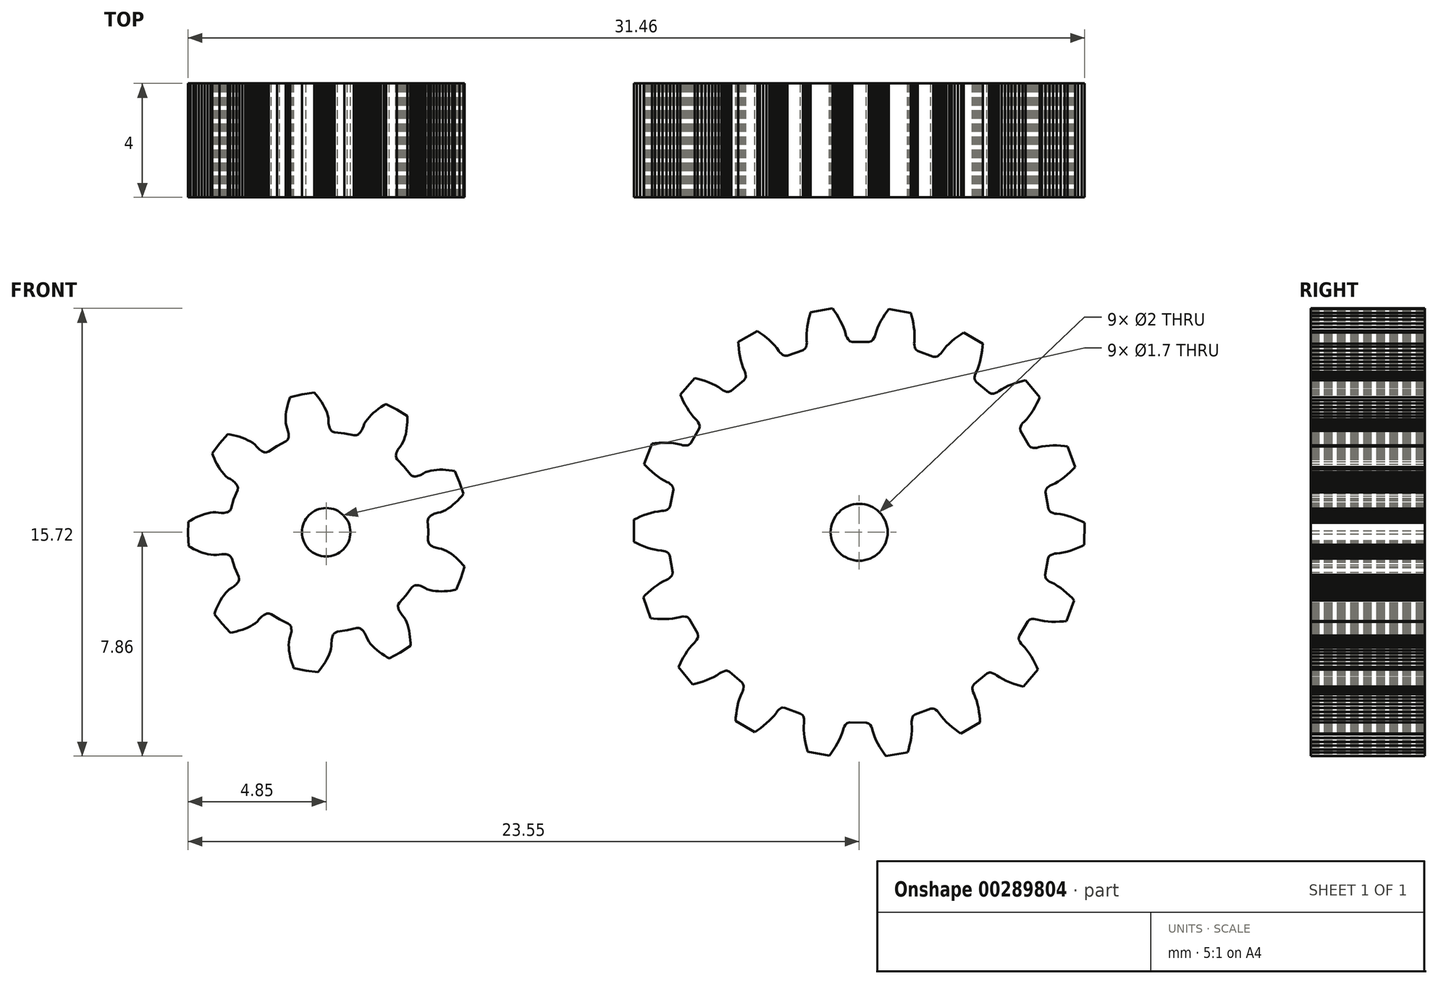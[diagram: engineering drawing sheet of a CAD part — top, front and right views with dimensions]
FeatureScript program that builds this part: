
annotation { "Feature Type Name" : "Feature", "Feature Type Description" : "" }
export const myFeature = defineFeature(function(context is Context, id is Id, definition is map)
    precondition{}
    {
        {
            var Q0;
            Q0=qCreatedBy(makeId("Front.planeOp"),FACE);
            var sketch = newSketch(context, id + "F0", { "sketchPlane" : qUnion([Q0])});
            skLineSegment(sketch, "E0", {"start": v(3.58, -0.29) * mm, "end": v(3.6, -0.37) * mm});
            skLineSegment(sketch, "E1", {"start": v(3.6, -0.37) * mm, "end": v(3.61, -0.4) * mm});
            skLineSegment(sketch, "E2", {"start": v(3.61, -0.4) * mm, "end": v(3.63, -0.43) * mm});
            skLineSegment(sketch, "E3", {"start": v(3.63, -0.43) * mm, "end": v(3.65, -0.45) * mm});
            skLineSegment(sketch, "E4", {"start": v(3.65, -0.45) * mm, "end": v(3.67, -0.46) * mm});
            skLineSegment(sketch, "E5", {"start": v(3.67, -0.46) * mm, "end": v(3.72, -0.5) * mm});
            skLineSegment(sketch, "E6", {"start": v(3.72, -0.5) * mm, "end": v(3.76, -0.51) * mm});
            skLineSegment(sketch, "E7", {"start": v(3.76, -0.51) * mm, "end": v(3.8, -0.53) * mm});
            skLineSegment(sketch, "E8", {"start": v(3.8, -0.53) * mm, "end": v(3.85, -0.54) * mm});
            skLineSegment(sketch, "E9", {"start": v(3.85, -0.54) * mm, "end": v(3.95, -0.56) * mm});
            skLineSegment(sketch, "E10", {"start": v(3.95, -0.56) * mm, "end": v(4.04, -0.58) * mm});
            skLineSegment(sketch, "E11", {"start": v(4.04, -0.58) * mm, "end": v(4.13, -0.61) * mm});
            skLineSegment(sketch, "E12", {"start": v(4.13, -0.61) * mm, "end": v(4.22, -0.66) * mm});
            skLineSegment(sketch, "E13", {"start": v(4.22, -0.66) * mm, "end": v(4.3, -0.7) * mm});
            skLineSegment(sketch, "E14", {"start": v(4.3, -0.7) * mm, "end": v(4.4, -0.76) * mm});
            skLineSegment(sketch, "E15", {"start": v(4.4, -0.76) * mm, "end": v(4.47, -0.83) * mm});
            skLineSegment(sketch, "E16", {"start": v(4.47, -0.83) * mm, "end": v(4.56, -0.9) * mm});
            skLineSegment(sketch, "E17", {"start": v(4.56, -0.9) * mm, "end": v(4.64, -0.97) * mm});
            skLineSegment(sketch, "E18", {"start": v(4.64, -0.97) * mm, "end": v(4.72, -1.05) * mm});
            skLineSegment(sketch, "E19", {"start": v(4.72, -1.05) * mm, "end": v(4.8, -1.13) * mm});
            skLineSegment(sketch, "E20", {"start": v(4.8, -1.13) * mm, "end": v(4.85, -1.2) * mm});
            skLineSegment(sketch, "E21", {"start": v(4.85, -1.2) * mm, "end": v(4.73, -1.61) * mm});
            skLineSegment(sketch, "E22", {"start": v(4.73, -1.61) * mm, "end": v(4.57, -2.01) * mm});
            skLineSegment(sketch, "E23", {"start": v(4.57, -2.01) * mm, "end": v(4.48, -2.03) * mm});
            skLineSegment(sketch, "E24", {"start": v(4.48, -2.03) * mm, "end": v(4.37, -2.05) * mm});
            skLineSegment(sketch, "E25", {"start": v(4.37, -2.05) * mm, "end": v(4.26, -2.06) * mm});
            skLineSegment(sketch, "E26", {"start": v(4.26, -2.06) * mm, "end": v(4.15, -2.07) * mm});
            skLineSegment(sketch, "E27", {"start": v(4.15, -2.07) * mm, "end": v(4.04, -2.07) * mm});
            skLineSegment(sketch, "E28", {"start": v(4.04, -2.07) * mm, "end": v(3.94, -2.07) * mm});
            skLineSegment(sketch, "E29", {"start": v(3.94, -2.07) * mm, "end": v(3.83, -2.06) * mm});
            skLineSegment(sketch, "E30", {"start": v(3.83, -2.06) * mm, "end": v(3.73, -2.05) * mm});
            skLineSegment(sketch, "E31", {"start": v(3.73, -2.05) * mm, "end": v(3.64, -2.03) * mm});
            skLineSegment(sketch, "E32", {"start": v(3.64, -2.03) * mm, "end": v(3.55, -2) * mm});
            skLineSegment(sketch, "E33", {"start": v(3.55, -2) * mm, "end": v(3.46, -1.95) * mm});
            skLineSegment(sketch, "E34", {"start": v(3.46, -1.95) * mm, "end": v(3.38, -1.9) * mm});
            skLineSegment(sketch, "E35", {"start": v(3.38, -1.9) * mm, "end": v(3.33, -1.9) * mm});
            skLineSegment(sketch, "E36", {"start": v(3.33, -1.9) * mm, "end": v(3.29, -1.88) * mm});
            skLineSegment(sketch, "E37", {"start": v(3.29, -1.88) * mm, "end": v(3.24, -1.87) * mm});
            skLineSegment(sketch, "E38", {"start": v(3.24, -1.87) * mm, "end": v(3.19, -1.86) * mm});
            skLineSegment(sketch, "E39", {"start": v(3.19, -1.86) * mm, "end": v(3.16, -1.86) * mm});
            skLineSegment(sketch, "E40", {"start": v(3.16, -1.86) * mm, "end": v(3.13, -1.86) * mm});
            skLineSegment(sketch, "E41", {"start": v(3.13, -1.86) * mm, "end": v(3.1, -1.87) * mm});
            skLineSegment(sketch, "E42", {"start": v(3.1, -1.87) * mm, "end": v(3.06, -1.88) * mm});
            skLineSegment(sketch, "E43", {"start": v(3.06, -1.88) * mm, "end": v(3, -1.94) * mm});
            skLineSegment(sketch, "E44", {"start": v(3, -1.94) * mm, "end": v(2.8, -2.21) * mm});
            skLineSegment(sketch, "E45", {"start": v(2.8, -2.21) * mm, "end": v(2.57, -2.47) * mm});
            skLineSegment(sketch, "E46", {"start": v(2.57, -2.47) * mm, "end": v(2.53, -2.54) * mm});
            skLineSegment(sketch, "E47", {"start": v(2.53, -2.54) * mm, "end": v(2.52, -2.58) * mm});
            skLineSegment(sketch, "E48", {"start": v(2.52, -2.58) * mm, "end": v(2.52, -2.61) * mm});
            skLineSegment(sketch, "E49", {"start": v(2.52, -2.61) * mm, "end": v(2.52, -2.64) * mm});
            skLineSegment(sketch, "E50", {"start": v(2.52, -2.64) * mm, "end": v(2.53, -2.67) * mm});
            skLineSegment(sketch, "E51", {"start": v(2.53, -2.67) * mm, "end": v(2.55, -2.72) * mm});
            skLineSegment(sketch, "E52", {"start": v(2.55, -2.72) * mm, "end": v(2.57, -2.76) * mm});
            skLineSegment(sketch, "E53", {"start": v(2.57, -2.76) * mm, "end": v(2.59, -2.8) * mm});
            skLineSegment(sketch, "E54", {"start": v(2.59, -2.8) * mm, "end": v(2.62, -2.84) * mm});
            skLineSegment(sketch, "E55", {"start": v(2.62, -2.84) * mm, "end": v(2.67, -2.92) * mm});
            skLineSegment(sketch, "E56", {"start": v(2.67, -2.92) * mm, "end": v(2.74, -3) * mm});
            skLineSegment(sketch, "E57", {"start": v(2.74, -3) * mm, "end": v(2.78, -3.07) * mm});
            skLineSegment(sketch, "E58", {"start": v(2.78, -3.07) * mm, "end": v(2.82, -3.16) * mm});
            skLineSegment(sketch, "E59", {"start": v(2.82, -3.16) * mm, "end": v(2.86, -3.26) * mm});
            skLineSegment(sketch, "E60", {"start": v(2.86, -3.26) * mm, "end": v(2.89, -3.36) * mm});
            skLineSegment(sketch, "E61", {"start": v(2.89, -3.36) * mm, "end": v(2.9, -3.46) * mm});
            skLineSegment(sketch, "E62", {"start": v(2.9, -3.46) * mm, "end": v(2.93, -3.57) * mm});
            skLineSegment(sketch, "E63", {"start": v(2.93, -3.57) * mm, "end": v(2.94, -3.68) * mm});
            skLineSegment(sketch, "E64", {"start": v(2.94, -3.68) * mm, "end": v(2.95, -3.79) * mm});
            skLineSegment(sketch, "E65", {"start": v(2.95, -3.79) * mm, "end": v(2.96, -3.9) * mm});
            skLineSegment(sketch, "E66", {"start": v(2.96, -3.9) * mm, "end": v(2.96, -3.99) * mm});
            skLineSegment(sketch, "E67", {"start": v(2.96, -3.99) * mm, "end": v(2.6, -4.23) * mm});
            skLineSegment(sketch, "E68", {"start": v(2.6, -4.23) * mm, "end": v(2.22, -4.43) * mm});
            skLineSegment(sketch, "E69", {"start": v(2.22, -4.43) * mm, "end": v(2.14, -4.39) * mm});
            skLineSegment(sketch, "E70", {"start": v(2.14, -4.39) * mm, "end": v(2.04, -4.33) * mm});
            skLineSegment(sketch, "E71", {"start": v(2.04, -4.33) * mm, "end": v(1.95, -4.27) * mm});
            skLineSegment(sketch, "E72", {"start": v(1.95, -4.27) * mm, "end": v(1.86, -4.2) * mm});
            skLineSegment(sketch, "E73", {"start": v(1.86, -4.2) * mm, "end": v(1.78, -4.14) * mm});
            skLineSegment(sketch, "E74", {"start": v(1.78, -4.14) * mm, "end": v(1.7, -4.07) * mm});
            skLineSegment(sketch, "E75", {"start": v(1.7, -4.07) * mm, "end": v(1.62, -4) * mm});
            skLineSegment(sketch, "E76", {"start": v(1.62, -4) * mm, "end": v(1.56, -3.92) * mm});
            skLineSegment(sketch, "E77", {"start": v(1.56, -3.92) * mm, "end": v(1.5, -3.84) * mm});
            skLineSegment(sketch, "E78", {"start": v(1.5, -3.84) * mm, "end": v(1.45, -3.76) * mm});
            skLineSegment(sketch, "E79", {"start": v(1.45, -3.76) * mm, "end": v(1.41, -3.67) * mm});
            skLineSegment(sketch, "E80", {"start": v(1.41, -3.67) * mm, "end": v(1.37, -3.59) * mm});
            skLineSegment(sketch, "E81", {"start": v(1.37, -3.59) * mm, "end": v(1.35, -3.54) * mm});
            skLineSegment(sketch, "E82", {"start": v(1.35, -3.54) * mm, "end": v(1.33, -3.5) * mm});
            skLineSegment(sketch, "E83", {"start": v(1.33, -3.5) * mm, "end": v(1.3, -3.46) * mm});
            skLineSegment(sketch, "E84", {"start": v(1.3, -3.46) * mm, "end": v(1.26, -3.43) * mm});
            skLineSegment(sketch, "E85", {"start": v(1.26, -3.43) * mm, "end": v(1.24, -3.4) * mm});
            skLineSegment(sketch, "E86", {"start": v(1.24, -3.4) * mm, "end": v(1.21, -3.4) * mm});
            skLineSegment(sketch, "E87", {"start": v(1.21, -3.4) * mm, "end": v(1.19, -3.38) * mm});
            skLineSegment(sketch, "E88", {"start": v(1.19, -3.38) * mm, "end": v(1.15, -3.36) * mm});
            skLineSegment(sketch, "E89", {"start": v(1.15, -3.36) * mm, "end": v(1.07, -3.36) * mm});
            skLineSegment(sketch, "E90", {"start": v(1.07, -3.36) * mm, "end": v(0.73, -3.44) * mm});
            skLineSegment(sketch, "E91", {"start": v(0.73, -3.44) * mm, "end": v(0.4, -3.5) * mm});
            skLineSegment(sketch, "E92", {"start": v(0.4, -3.5) * mm, "end": v(0.31, -3.52) * mm});
            skLineSegment(sketch, "E93", {"start": v(0.31, -3.52) * mm, "end": v(0.29, -3.55) * mm});
            skLineSegment(sketch, "E94", {"start": v(0.29, -3.55) * mm, "end": v(0.27, -3.57) * mm});
            skLineSegment(sketch, "E95", {"start": v(0.27, -3.57) * mm, "end": v(0.25, -3.6) * mm});
            skLineSegment(sketch, "E96", {"start": v(0.25, -3.6) * mm, "end": v(0.24, -3.62) * mm});
            skLineSegment(sketch, "E97", {"start": v(0.24, -3.62) * mm, "end": v(0.22, -3.67) * mm});
            skLineSegment(sketch, "E98", {"start": v(0.22, -3.67) * mm, "end": v(0.2, -3.72) * mm});
            skLineSegment(sketch, "E99", {"start": v(0.2, -3.72) * mm, "end": v(0.2, -3.76) * mm});
            skLineSegment(sketch, "E100", {"start": v(0.2, -3.76) * mm, "end": v(0.19, -3.81) * mm});
            skLineSegment(sketch, "E101", {"start": v(0.19, -3.81) * mm, "end": v(0.19, -3.9) * mm});
            skLineSegment(sketch, "E102", {"start": v(0.19, -3.9) * mm, "end": v(0.19, -4) * mm});
            skLineSegment(sketch, "E103", {"start": v(0.19, -4) * mm, "end": v(0.17, -4.1) * mm});
            skLineSegment(sketch, "E104", {"start": v(0.17, -4.1) * mm, "end": v(0.14, -4.19) * mm});
            skLineSegment(sketch, "E105", {"start": v(0.14, -4.19) * mm, "end": v(0.1, -4.28) * mm});
            skLineSegment(sketch, "E106", {"start": v(0.1, -4.28) * mm, "end": v(0.07, -4.38) * mm});
            skLineSegment(sketch, "E107", {"start": v(0.07, -4.38) * mm, "end": v(0.02, -4.47) * mm});
            skLineSegment(sketch, "E108", {"start": v(0.02, -4.47) * mm, "end": v(-0.04, -4.57) * mm});
            skLineSegment(sketch, "E109", {"start": v(-0.04, -4.57) * mm, "end": v(-0.1, -4.66) * mm});
            skLineSegment(sketch, "E110", {"start": v(-0.1, -4.66) * mm, "end": v(-0.16, -4.75) * mm});
            skLineSegment(sketch, "E111", {"start": v(-0.16, -4.75) * mm, "end": v(-0.23, -4.84) * mm});
            skLineSegment(sketch, "E112", {"start": v(-0.23, -4.84) * mm, "end": v(-0.28, -4.9) * mm});
            skLineSegment(sketch, "E113", {"start": v(-0.28, -4.9) * mm, "end": v(-0.71, -4.86) * mm});
            skLineSegment(sketch, "E114", {"start": v(-0.71, -4.86) * mm, "end": v(-1.13, -4.77) * mm});
            skLineSegment(sketch, "E115", {"start": v(-1.13, -4.77) * mm, "end": v(-1.17, -4.69) * mm});
            skLineSegment(sketch, "E116", {"start": v(-1.17, -4.69) * mm, "end": v(-1.2, -4.58) * mm});
            skLineSegment(sketch, "E117", {"start": v(-1.2, -4.58) * mm, "end": v(-1.24, -4.47) * mm});
            skLineSegment(sketch, "E118", {"start": v(-1.24, -4.47) * mm, "end": v(-1.26, -4.37) * mm});
            skLineSegment(sketch, "E119", {"start": v(-1.26, -4.37) * mm, "end": v(-1.28, -4.26) * mm});
            skLineSegment(sketch, "E120", {"start": v(-1.28, -4.26) * mm, "end": v(-1.3, -4.16) * mm});
            skLineSegment(sketch, "E121", {"start": v(-1.3, -4.16) * mm, "end": v(-1.3, -4.05) * mm});
            skLineSegment(sketch, "E122", {"start": v(-1.3, -4.05) * mm, "end": v(-1.31, -3.95) * mm});
            skLineSegment(sketch, "E123", {"start": v(-1.31, -3.95) * mm, "end": v(-1.3, -3.86) * mm});
            skLineSegment(sketch, "E124", {"start": v(-1.3, -3.86) * mm, "end": v(-1.3, -3.76) * mm});
            skLineSegment(sketch, "E125", {"start": v(-1.3, -3.76) * mm, "end": v(-1.27, -3.67) * mm});
            skLineSegment(sketch, "E126", {"start": v(-1.27, -3.67) * mm, "end": v(-1.24, -3.58) * mm});
            skLineSegment(sketch, "E127", {"start": v(-1.24, -3.58) * mm, "end": v(-1.23, -3.53) * mm});
            skLineSegment(sketch, "E128", {"start": v(-1.23, -3.53) * mm, "end": v(-1.22, -3.49) * mm});
            skLineSegment(sketch, "E129", {"start": v(-1.22, -3.49) * mm, "end": v(-1.22, -3.44) * mm});
            skLineSegment(sketch, "E130", {"start": v(-1.22, -3.44) * mm, "end": v(-1.22, -3.38) * mm});
            skLineSegment(sketch, "E131", {"start": v(-1.22, -3.38) * mm, "end": v(-1.23, -3.36) * mm});
            skLineSegment(sketch, "E132", {"start": v(-1.23, -3.36) * mm, "end": v(-1.24, -3.33) * mm});
            skLineSegment(sketch, "E133", {"start": v(-1.24, -3.33) * mm, "end": v(-1.25, -3.3) * mm});
            skLineSegment(sketch, "E134", {"start": v(-1.25, -3.3) * mm, "end": v(-1.27, -3.27) * mm});
            skLineSegment(sketch, "E135", {"start": v(-1.27, -3.27) * mm, "end": v(-1.33, -3.21) * mm});
            skLineSegment(sketch, "E136", {"start": v(-1.33, -3.21) * mm, "end": v(-1.64, -3.06) * mm});
            skLineSegment(sketch, "E137", {"start": v(-1.64, -3.06) * mm, "end": v(-1.93, -2.88) * mm});
            skLineSegment(sketch, "E138", {"start": v(-1.93, -2.88) * mm, "end": v(-2, -2.85) * mm});
            skLineSegment(sketch, "E139", {"start": v(-2, -2.85) * mm, "end": v(-2.05, -2.85) * mm});
            skLineSegment(sketch, "E140", {"start": v(-2.05, -2.85) * mm, "end": v(-2.08, -2.86) * mm});
            skLineSegment(sketch, "E141", {"start": v(-2.08, -2.86) * mm, "end": v(-2.1, -2.87) * mm});
            skLineSegment(sketch, "E142", {"start": v(-2.1, -2.87) * mm, "end": v(-2.13, -2.88) * mm});
            skLineSegment(sketch, "E143", {"start": v(-2.13, -2.88) * mm, "end": v(-2.18, -2.9) * mm});
            skLineSegment(sketch, "E144", {"start": v(-2.18, -2.9) * mm, "end": v(-2.22, -2.93) * mm});
            skLineSegment(sketch, "E145", {"start": v(-2.22, -2.93) * mm, "end": v(-2.26, -2.96) * mm});
            skLineSegment(sketch, "E146", {"start": v(-2.26, -2.96) * mm, "end": v(-2.3, -3) * mm});
            skLineSegment(sketch, "E147", {"start": v(-2.3, -3) * mm, "end": v(-2.35, -3.06) * mm});
            skLineSegment(sketch, "E148", {"start": v(-2.35, -3.06) * mm, "end": v(-2.41, -3.13) * mm});
            skLineSegment(sketch, "E149", {"start": v(-2.41, -3.13) * mm, "end": v(-2.49, -3.2) * mm});
            skLineSegment(sketch, "E150", {"start": v(-2.49, -3.2) * mm, "end": v(-2.57, -3.25) * mm});
            skLineSegment(sketch, "E151", {"start": v(-2.57, -3.25) * mm, "end": v(-2.66, -3.3) * mm});
            skLineSegment(sketch, "E152", {"start": v(-2.66, -3.3) * mm, "end": v(-2.75, -3.35) * mm});
            skLineSegment(sketch, "E153", {"start": v(-2.75, -3.35) * mm, "end": v(-2.85, -3.39) * mm});
            skLineSegment(sketch, "E154", {"start": v(-2.85, -3.39) * mm, "end": v(-2.95, -3.42) * mm});
            skLineSegment(sketch, "E155", {"start": v(-2.95, -3.42) * mm, "end": v(-3.05, -3.46) * mm});
            skLineSegment(sketch, "E156", {"start": v(-3.05, -3.46) * mm, "end": v(-3.16, -3.49) * mm});
            skLineSegment(sketch, "E157", {"start": v(-3.16, -3.49) * mm, "end": v(-3.27, -3.51) * mm});
            skLineSegment(sketch, "E158", {"start": v(-3.27, -3.51) * mm, "end": v(-3.36, -3.53) * mm});
            skLineSegment(sketch, "E159", {"start": v(-3.36, -3.53) * mm, "end": v(-3.65, -3.21) * mm});
            skLineSegment(sketch, "E160", {"start": v(-3.65, -3.21) * mm, "end": v(-3.92, -2.87) * mm});
            skLineSegment(sketch, "E161", {"start": v(-3.92, -2.87) * mm, "end": v(-3.9, -2.8) * mm});
            skLineSegment(sketch, "E162", {"start": v(-3.9, -2.8) * mm, "end": v(-3.85, -2.69) * mm});
            skLineSegment(sketch, "E163", {"start": v(-3.85, -2.69) * mm, "end": v(-3.8, -2.58) * mm});
            skLineSegment(sketch, "E164", {"start": v(-3.8, -2.58) * mm, "end": v(-3.76, -2.48) * mm});
            skLineSegment(sketch, "E165", {"start": v(-3.76, -2.48) * mm, "end": v(-3.7, -2.39) * mm});
            skLineSegment(sketch, "E166", {"start": v(-3.7, -2.39) * mm, "end": v(-3.65, -2.3) * mm});
            skLineSegment(sketch, "E167", {"start": v(-3.65, -2.3) * mm, "end": v(-3.6, -2.21) * mm});
            skLineSegment(sketch, "E168", {"start": v(-3.6, -2.21) * mm, "end": v(-3.53, -2.14) * mm});
            skLineSegment(sketch, "E169", {"start": v(-3.53, -2.14) * mm, "end": v(-3.47, -2.06) * mm});
            skLineSegment(sketch, "E170", {"start": v(-3.47, -2.06) * mm, "end": v(-3.4, -2) * mm});
            skLineSegment(sketch, "E171", {"start": v(-3.4, -2) * mm, "end": v(-3.32, -1.95) * mm});
            skLineSegment(sketch, "E172", {"start": v(-3.32, -1.95) * mm, "end": v(-3.24, -1.9) * mm});
            skLineSegment(sketch, "E173", {"start": v(-3.24, -1.9) * mm, "end": v(-3.2, -1.87) * mm});
            skLineSegment(sketch, "E174", {"start": v(-3.2, -1.87) * mm, "end": v(-3.16, -1.83) * mm});
            skLineSegment(sketch, "E175", {"start": v(-3.16, -1.83) * mm, "end": v(-3.13, -1.8) * mm});
            skLineSegment(sketch, "E176", {"start": v(-3.13, -1.8) * mm, "end": v(-3.1, -1.76) * mm});
            skLineSegment(sketch, "E177", {"start": v(-3.1, -1.76) * mm, "end": v(-3.09, -1.73) * mm});
            skLineSegment(sketch, "E178", {"start": v(-3.09, -1.73) * mm, "end": v(-3.07, -1.7) * mm});
            skLineSegment(sketch, "E179", {"start": v(-3.07, -1.7) * mm, "end": v(-3.06, -1.68) * mm});
            skLineSegment(sketch, "E180", {"start": v(-3.06, -1.68) * mm, "end": v(-3.06, -1.64) * mm});
            skLineSegment(sketch, "E181", {"start": v(-3.06, -1.64) * mm, "end": v(-3.07, -1.56) * mm});
            skLineSegment(sketch, "E182", {"start": v(-3.07, -1.56) * mm, "end": v(-3.2, -1.24) * mm});
            skLineSegment(sketch, "E183", {"start": v(-3.2, -1.24) * mm, "end": v(-3.32, -0.91) * mm});
            skLineSegment(sketch, "E184", {"start": v(-3.32, -0.91) * mm, "end": v(-3.36, -0.84) * mm});
            skLineSegment(sketch, "E185", {"start": v(-3.36, -0.84) * mm, "end": v(-3.39, -0.82) * mm});
            skLineSegment(sketch, "E186", {"start": v(-3.39, -0.82) * mm, "end": v(-3.42, -0.8) * mm});
            skLineSegment(sketch, "E187", {"start": v(-3.42, -0.8) * mm, "end": v(-3.44, -0.8) * mm});
            skLineSegment(sketch, "E188", {"start": v(-3.44, -0.8) * mm, "end": v(-3.47, -0.78) * mm});
            skLineSegment(sketch, "E189", {"start": v(-3.47, -0.78) * mm, "end": v(-3.52, -0.77) * mm});
            skLineSegment(sketch, "E190", {"start": v(-3.52, -0.77) * mm, "end": v(-3.57, -0.77) * mm});
            skLineSegment(sketch, "E191", {"start": v(-3.57, -0.77) * mm, "end": v(-3.62, -0.77) * mm});
            skLineSegment(sketch, "E192", {"start": v(-3.62, -0.77) * mm, "end": v(-3.66, -0.77) * mm});
            skLineSegment(sketch, "E193", {"start": v(-3.66, -0.77) * mm, "end": v(-3.76, -0.78) * mm});
            skLineSegment(sketch, "E194", {"start": v(-3.76, -0.78) * mm, "end": v(-3.85, -0.8) * mm});
            skLineSegment(sketch, "E195", {"start": v(-3.85, -0.8) * mm, "end": v(-3.95, -0.8) * mm});
            skLineSegment(sketch, "E196", {"start": v(-3.95, -0.8) * mm, "end": v(-4.04, -0.79) * mm});
            skLineSegment(sketch, "E197", {"start": v(-4.04, -0.79) * mm, "end": v(-4.14, -0.77) * mm});
            skLineSegment(sketch, "E198", {"start": v(-4.14, -0.77) * mm, "end": v(-4.24, -0.75) * mm});
            skLineSegment(sketch, "E199", {"start": v(-4.24, -0.75) * mm, "end": v(-4.34, -0.72) * mm});
            skLineSegment(sketch, "E200", {"start": v(-4.34, -0.72) * mm, "end": v(-4.45, -0.68) * mm});
            skLineSegment(sketch, "E201", {"start": v(-4.45, -0.68) * mm, "end": v(-4.55, -0.64) * mm});
            skLineSegment(sketch, "E202", {"start": v(-4.55, -0.64) * mm, "end": v(-4.65, -0.59) * mm});
            skLineSegment(sketch, "E203", {"start": v(-4.65, -0.59) * mm, "end": v(-4.75, -0.54) * mm});
            skLineSegment(sketch, "E204", {"start": v(-4.75, -0.54) * mm, "end": v(-4.83, -0.5) * mm});
            skLineSegment(sketch, "E205", {"start": v(-4.83, -0.5) * mm, "end": v(-4.85, -0.06) * mm});
            skLineSegment(sketch, "E206", {"start": v(-4.85, -0.06) * mm, "end": v(-4.84, 0.37) * mm});
            skLineSegment(sketch, "E207", {"start": v(-4.84, 0.37) * mm, "end": v(-4.76, 0.41) * mm});
            skLineSegment(sketch, "E208", {"start": v(-4.76, 0.41) * mm, "end": v(-4.66, 0.47) * mm});
            skLineSegment(sketch, "E209", {"start": v(-4.66, 0.47) * mm, "end": v(-4.56, 0.52) * mm});
            skLineSegment(sketch, "E210", {"start": v(-4.56, 0.52) * mm, "end": v(-4.46, 0.56) * mm});
            skLineSegment(sketch, "E211", {"start": v(-4.46, 0.56) * mm, "end": v(-4.36, 0.6) * mm});
            skLineSegment(sketch, "E212", {"start": v(-4.36, 0.6) * mm, "end": v(-4.26, 0.64) * mm});
            skLineSegment(sketch, "E213", {"start": v(-4.26, 0.64) * mm, "end": v(-4.16, 0.66) * mm});
            skLineSegment(sketch, "E214", {"start": v(-4.16, 0.66) * mm, "end": v(-4.07, 0.69) * mm});
            skLineSegment(sketch, "E215", {"start": v(-4.07, 0.69) * mm, "end": v(-3.97, 0.7) * mm});
            skLineSegment(sketch, "E216", {"start": v(-3.97, 0.7) * mm, "end": v(-3.87, 0.7) * mm});
            skLineSegment(sketch, "E217", {"start": v(-3.87, 0.7) * mm, "end": v(-3.78, 0.69) * mm});
            skLineSegment(sketch, "E218", {"start": v(-3.78, 0.69) * mm, "end": v(-3.68, 0.68) * mm});
            skLineSegment(sketch, "E219", {"start": v(-3.68, 0.68) * mm, "end": v(-3.64, 0.67) * mm});
            skLineSegment(sketch, "E220", {"start": v(-3.64, 0.67) * mm, "end": v(-3.59, 0.68) * mm});
            skLineSegment(sketch, "E221", {"start": v(-3.59, 0.68) * mm, "end": v(-3.54, 0.68) * mm});
            skLineSegment(sketch, "E222", {"start": v(-3.54, 0.68) * mm, "end": v(-3.49, 0.7) * mm});
            skLineSegment(sketch, "E223", {"start": v(-3.49, 0.7) * mm, "end": v(-3.46, 0.7) * mm});
            skLineSegment(sketch, "E224", {"start": v(-3.46, 0.7) * mm, "end": v(-3.44, 0.72) * mm});
            skLineSegment(sketch, "E225", {"start": v(-3.44, 0.72) * mm, "end": v(-3.4, 0.73) * mm});
            skLineSegment(sketch, "E226", {"start": v(-3.4, 0.73) * mm, "end": v(-3.38, 0.76) * mm});
            skLineSegment(sketch, "E227", {"start": v(-3.38, 0.76) * mm, "end": v(-3.34, 0.83) * mm});
            skLineSegment(sketch, "E228", {"start": v(-3.34, 0.83) * mm, "end": v(-3.24, 1.16) * mm});
            skLineSegment(sketch, "E229", {"start": v(-3.24, 1.16) * mm, "end": v(-3.11, 1.48) * mm});
            skLineSegment(sketch, "E230", {"start": v(-3.11, 1.48) * mm, "end": v(-3.1, 1.56) * mm});
            skLineSegment(sketch, "E231", {"start": v(-3.1, 1.56) * mm, "end": v(-3.1, 1.6) * mm});
            skLineSegment(sketch, "E232", {"start": v(-3.1, 1.6) * mm, "end": v(-3.12, 1.63) * mm});
            skLineSegment(sketch, "E233", {"start": v(-3.12, 1.63) * mm, "end": v(-3.13, 1.66) * mm});
            skLineSegment(sketch, "E234", {"start": v(-3.13, 1.66) * mm, "end": v(-3.15, 1.68) * mm});
            skLineSegment(sketch, "E235", {"start": v(-3.15, 1.68) * mm, "end": v(-3.18, 1.72) * mm});
            skLineSegment(sketch, "E236", {"start": v(-3.18, 1.72) * mm, "end": v(-3.21, 1.76) * mm});
            skLineSegment(sketch, "E237", {"start": v(-3.21, 1.76) * mm, "end": v(-3.25, 1.79) * mm});
            skLineSegment(sketch, "E238", {"start": v(-3.25, 1.79) * mm, "end": v(-3.29, 1.82) * mm});
            skLineSegment(sketch, "E239", {"start": v(-3.29, 1.82) * mm, "end": v(-3.37, 1.87) * mm});
            skLineSegment(sketch, "E240", {"start": v(-3.37, 1.87) * mm, "end": v(-3.45, 1.91) * mm});
            skLineSegment(sketch, "E241", {"start": v(-3.45, 1.91) * mm, "end": v(-3.52, 1.97) * mm});
            skLineSegment(sketch, "E242", {"start": v(-3.52, 1.97) * mm, "end": v(-3.6, 2.05) * mm});
            skLineSegment(sketch, "E243", {"start": v(-3.6, 2.05) * mm, "end": v(-3.66, 2.12) * mm});
            skLineSegment(sketch, "E244", {"start": v(-3.66, 2.12) * mm, "end": v(-3.72, 2.2) * mm});
            skLineSegment(sketch, "E245", {"start": v(-3.72, 2.2) * mm, "end": v(-3.77, 2.3) * mm});
            skLineSegment(sketch, "E246", {"start": v(-3.77, 2.3) * mm, "end": v(-3.83, 2.39) * mm});
            skLineSegment(sketch, "E247", {"start": v(-3.83, 2.39) * mm, "end": v(-3.88, 2.48) * mm});
            skLineSegment(sketch, "E248", {"start": v(-3.88, 2.48) * mm, "end": v(-3.93, 2.59) * mm});
            skLineSegment(sketch, "E249", {"start": v(-3.93, 2.59) * mm, "end": v(-3.97, 2.7) * mm});
            skLineSegment(sketch, "E250", {"start": v(-3.97, 2.7) * mm, "end": v(-4, 2.77) * mm});
            skLineSegment(sketch, "E251", {"start": v(-4, 2.77) * mm, "end": v(-3.74, 3.12) * mm});
            skLineSegment(sketch, "E252", {"start": v(-3.74, 3.12) * mm, "end": v(-3.46, 3.44) * mm});
            skLineSegment(sketch, "E253", {"start": v(-3.46, 3.44) * mm, "end": v(-3.37, 3.43) * mm});
            skLineSegment(sketch, "E254", {"start": v(-3.37, 3.43) * mm, "end": v(-3.26, 3.4) * mm});
            skLineSegment(sketch, "E255", {"start": v(-3.26, 3.4) * mm, "end": v(-3.15, 3.38) * mm});
            skLineSegment(sketch, "E256", {"start": v(-3.15, 3.38) * mm, "end": v(-3.04, 3.35) * mm});
            skLineSegment(sketch, "E257", {"start": v(-3.04, 3.35) * mm, "end": v(-2.94, 3.32) * mm});
            skLineSegment(sketch, "E258", {"start": v(-2.94, 3.32) * mm, "end": v(-2.84, 3.28) * mm});
            skLineSegment(sketch, "E259", {"start": v(-2.84, 3.28) * mm, "end": v(-2.75, 3.24) * mm});
            skLineSegment(sketch, "E260", {"start": v(-2.75, 3.24) * mm, "end": v(-2.66, 3.19) * mm});
            skLineSegment(sketch, "E261", {"start": v(-2.66, 3.19) * mm, "end": v(-2.58, 3.13) * mm});
            skLineSegment(sketch, "E262", {"start": v(-2.58, 3.13) * mm, "end": v(-2.5, 3.08) * mm});
            skLineSegment(sketch, "E263", {"start": v(-2.5, 3.08) * mm, "end": v(-2.44, 3) * mm});
            skLineSegment(sketch, "E264", {"start": v(-2.44, 3) * mm, "end": v(-2.37, 2.94) * mm});
            skLineSegment(sketch, "E265", {"start": v(-2.37, 2.94) * mm, "end": v(-2.34, 2.9) * mm});
            skLineSegment(sketch, "E266", {"start": v(-2.34, 2.9) * mm, "end": v(-2.3, 2.87) * mm});
            skLineSegment(sketch, "E267", {"start": v(-2.3, 2.87) * mm, "end": v(-2.26, 2.85) * mm});
            skLineSegment(sketch, "E268", {"start": v(-2.26, 2.85) * mm, "end": v(-2.21, 2.83) * mm});
            skLineSegment(sketch, "E269", {"start": v(-2.21, 2.83) * mm, "end": v(-2.19, 2.82) * mm});
            skLineSegment(sketch, "E270", {"start": v(-2.19, 2.82) * mm, "end": v(-2.16, 2.8) * mm});
            skLineSegment(sketch, "E271", {"start": v(-2.16, 2.8) * mm, "end": v(-2.13, 2.8) * mm});
            skLineSegment(sketch, "E272", {"start": v(-2.13, 2.8) * mm, "end": v(-2.09, 2.8) * mm});
            skLineSegment(sketch, "E273", {"start": v(-2.09, 2.8) * mm, "end": v(-2.01, 2.83) * mm});
            skLineSegment(sketch, "E274", {"start": v(-2.01, 2.83) * mm, "end": v(-1.72, 3.02) * mm});
            skLineSegment(sketch, "E275", {"start": v(-1.72, 3.02) * mm, "end": v(-1.42, 3.19) * mm});
            skLineSegment(sketch, "E276", {"start": v(-1.42, 3.19) * mm, "end": v(-1.36, 3.24) * mm});
            skLineSegment(sketch, "E277", {"start": v(-1.36, 3.24) * mm, "end": v(-1.34, 3.27) * mm});
            skLineSegment(sketch, "E278", {"start": v(-1.34, 3.27) * mm, "end": v(-1.33, 3.3) * mm});
            skLineSegment(sketch, "E279", {"start": v(-1.33, 3.3) * mm, "end": v(-1.32, 3.33) * mm});
            skLineSegment(sketch, "E280", {"start": v(-1.32, 3.33) * mm, "end": v(-1.32, 3.36) * mm});
            skLineSegment(sketch, "E281", {"start": v(-1.32, 3.36) * mm, "end": v(-1.32, 3.41) * mm});
            skLineSegment(sketch, "E282", {"start": v(-1.32, 3.41) * mm, "end": v(-1.32, 3.46) * mm});
            skLineSegment(sketch, "E283", {"start": v(-1.32, 3.46) * mm, "end": v(-1.33, 3.5) * mm});
            skLineSegment(sketch, "E284", {"start": v(-1.33, 3.5) * mm, "end": v(-1.34, 3.55) * mm});
            skLineSegment(sketch, "E285", {"start": v(-1.34, 3.55) * mm, "end": v(-1.37, 3.64) * mm});
            skLineSegment(sketch, "E286", {"start": v(-1.37, 3.64) * mm, "end": v(-1.4, 3.73) * mm});
            skLineSegment(sketch, "E287", {"start": v(-1.4, 3.73) * mm, "end": v(-1.42, 3.83) * mm});
            skLineSegment(sketch, "E288", {"start": v(-1.42, 3.83) * mm, "end": v(-1.42, 3.93) * mm});
            skLineSegment(sketch, "E289", {"start": v(-1.42, 3.93) * mm, "end": v(-1.42, 4.03) * mm});
            skLineSegment(sketch, "E290", {"start": v(-1.42, 4.03) * mm, "end": v(-1.42, 4.13) * mm});
            skLineSegment(sketch, "E291", {"start": v(-1.42, 4.13) * mm, "end": v(-1.4, 4.23) * mm});
            skLineSegment(sketch, "E292", {"start": v(-1.4, 4.23) * mm, "end": v(-1.38, 4.34) * mm});
            skLineSegment(sketch, "E293", {"start": v(-1.38, 4.34) * mm, "end": v(-1.36, 4.45) * mm});
            skLineSegment(sketch, "E294", {"start": v(-1.36, 4.45) * mm, "end": v(-1.33, 4.55) * mm});
            skLineSegment(sketch, "E295", {"start": v(-1.33, 4.55) * mm, "end": v(-1.3, 4.66) * mm});
            skLineSegment(sketch, "E296", {"start": v(-1.3, 4.66) * mm, "end": v(-1.27, 4.75) * mm});
            skLineSegment(sketch, "E297", {"start": v(-1.27, 4.75) * mm, "end": v(-0.85, 4.84) * mm});
            skLineSegment(sketch, "E298", {"start": v(-0.85, 4.84) * mm, "end": v(-0.42, 4.9) * mm});
            skLineSegment(sketch, "E299", {"start": v(-0.42, 4.9) * mm, "end": v(-0.36, 4.84) * mm});
            skLineSegment(sketch, "E300", {"start": v(-0.36, 4.84) * mm, "end": v(-0.3, 4.75) * mm});
            skLineSegment(sketch, "E301", {"start": v(-0.3, 4.75) * mm, "end": v(-0.22, 4.66) * mm});
            skLineSegment(sketch, "E302", {"start": v(-0.22, 4.66) * mm, "end": v(-0.16, 4.57) * mm});
            skLineSegment(sketch, "E303", {"start": v(-0.16, 4.57) * mm, "end": v(-0.1, 4.48) * mm});
            skLineSegment(sketch, "E304", {"start": v(-0.1, 4.48) * mm, "end": v(-0.06, 4.39) * mm});
            skLineSegment(sketch, "E305", {"start": v(-0.06, 4.39) * mm, "end": v(-0.01, 4.3) * mm});
            skLineSegment(sketch, "E306", {"start": v(-0.01, 4.3) * mm, "end": v(0.02, 4.2) * mm});
            skLineSegment(sketch, "E307", {"start": v(0.02, 4.2) * mm, "end": v(0.05, 4.1) * mm});
            skLineSegment(sketch, "E308", {"start": v(0.05, 4.1) * mm, "end": v(0.07, 4.01) * mm});
            skLineSegment(sketch, "E309", {"start": v(0.07, 4.01) * mm, "end": v(0.08, 3.92) * mm});
            skLineSegment(sketch, "E310", {"start": v(0.08, 3.92) * mm, "end": v(0.08, 3.82) * mm});
            skLineSegment(sketch, "E311", {"start": v(0.08, 3.82) * mm, "end": v(0.09, 3.78) * mm});
            skLineSegment(sketch, "E312", {"start": v(0.09, 3.78) * mm, "end": v(0.1, 3.73) * mm});
            skLineSegment(sketch, "E313", {"start": v(0.1, 3.73) * mm, "end": v(0.11, 3.68) * mm});
            skLineSegment(sketch, "E314", {"start": v(0.11, 3.68) * mm, "end": v(0.14, 3.64) * mm});
            skLineSegment(sketch, "E315", {"start": v(0.14, 3.64) * mm, "end": v(0.15, 3.61) * mm});
            skLineSegment(sketch, "E316", {"start": v(0.15, 3.61) * mm, "end": v(0.17, 3.59) * mm});
            skLineSegment(sketch, "E317", {"start": v(0.17, 3.59) * mm, "end": v(0.19, 3.56) * mm});
            skLineSegment(sketch, "E318", {"start": v(0.19, 3.56) * mm, "end": v(0.22, 3.54) * mm});
            skLineSegment(sketch, "E319", {"start": v(0.22, 3.54) * mm, "end": v(0.3, 3.51) * mm});
            skLineSegment(sketch, "E320", {"start": v(0.3, 3.51) * mm, "end": v(0.64, 3.47) * mm});
            skLineSegment(sketch, "E321", {"start": v(0.64, 3.47) * mm, "end": v(0.97, 3.4) * mm});
            skLineSegment(sketch, "E322", {"start": v(0.97, 3.4) * mm, "end": v(1.06, 3.4) * mm});
            skLineSegment(sketch, "E323", {"start": v(1.06, 3.4) * mm, "end": v(1.1, 3.42) * mm});
            skLineSegment(sketch, "E324", {"start": v(1.1, 3.42) * mm, "end": v(1.12, 3.43) * mm});
            skLineSegment(sketch, "E325", {"start": v(1.12, 3.43) * mm, "end": v(1.14, 3.45) * mm});
            skLineSegment(sketch, "E326", {"start": v(1.14, 3.45) * mm, "end": v(1.16, 3.47) * mm});
            skLineSegment(sketch, "E327", {"start": v(1.16, 3.47) * mm, "end": v(1.2, 3.5) * mm});
            skLineSegment(sketch, "E328", {"start": v(1.2, 3.5) * mm, "end": v(1.23, 3.55) * mm});
            skLineSegment(sketch, "E329", {"start": v(1.23, 3.55) * mm, "end": v(1.25, 3.59) * mm});
            skLineSegment(sketch, "E330", {"start": v(1.25, 3.59) * mm, "end": v(1.27, 3.63) * mm});
            skLineSegment(sketch, "E331", {"start": v(1.27, 3.63) * mm, "end": v(1.3, 3.72) * mm});
            skLineSegment(sketch, "E332", {"start": v(1.3, 3.72) * mm, "end": v(1.34, 3.8) * mm});
            skLineSegment(sketch, "E333", {"start": v(1.34, 3.8) * mm, "end": v(1.39, 3.9) * mm});
            skLineSegment(sketch, "E334", {"start": v(1.39, 3.9) * mm, "end": v(1.45, 3.97) * mm});
            skLineSegment(sketch, "E335", {"start": v(1.45, 3.97) * mm, "end": v(1.51, 4.05) * mm});
            skLineSegment(sketch, "E336", {"start": v(1.51, 4.05) * mm, "end": v(1.58, 4.12) * mm});
            skLineSegment(sketch, "E337", {"start": v(1.58, 4.12) * mm, "end": v(1.66, 4.2) * mm});
            skLineSegment(sketch, "E338", {"start": v(1.66, 4.2) * mm, "end": v(1.74, 4.26) * mm});
            skLineSegment(sketch, "E339", {"start": v(1.74, 4.26) * mm, "end": v(1.83, 4.33) * mm});
            skLineSegment(sketch, "E340", {"start": v(1.83, 4.33) * mm, "end": v(1.92, 4.4) * mm});
            skLineSegment(sketch, "E341", {"start": v(1.92, 4.4) * mm, "end": v(2.02, 4.46) * mm});
            skLineSegment(sketch, "E342", {"start": v(2.02, 4.46) * mm, "end": v(2.1, 4.5) * mm});
            skLineSegment(sketch, "E343", {"start": v(2.1, 4.5) * mm, "end": v(2.48, 4.3) * mm});
            skLineSegment(sketch, "E344", {"start": v(2.48, 4.3) * mm, "end": v(2.84, 4.08) * mm});
            skLineSegment(sketch, "E345", {"start": v(2.84, 4.08) * mm, "end": v(2.85, 4) * mm});
            skLineSegment(sketch, "E346", {"start": v(2.85, 4) * mm, "end": v(2.85, 3.88) * mm});
            skLineSegment(sketch, "E347", {"start": v(2.85, 3.88) * mm, "end": v(2.84, 3.77) * mm});
            skLineSegment(sketch, "E348", {"start": v(2.84, 3.77) * mm, "end": v(2.83, 3.66) * mm});
            skLineSegment(sketch, "E349", {"start": v(2.83, 3.66) * mm, "end": v(2.81, 3.55) * mm});
            skLineSegment(sketch, "E350", {"start": v(2.81, 3.55) * mm, "end": v(2.8, 3.45) * mm});
            skLineSegment(sketch, "E351", {"start": v(2.8, 3.45) * mm, "end": v(2.76, 3.35) * mm});
            skLineSegment(sketch, "E352", {"start": v(2.76, 3.35) * mm, "end": v(2.73, 3.25) * mm});
            skLineSegment(sketch, "E353", {"start": v(2.73, 3.25) * mm, "end": v(2.7, 3.16) * mm});
            skLineSegment(sketch, "E354", {"start": v(2.7, 3.16) * mm, "end": v(2.65, 3.08) * mm});
            skLineSegment(sketch, "E355", {"start": v(2.65, 3.08) * mm, "end": v(2.6, 3) * mm});
            skLineSegment(sketch, "E356", {"start": v(2.6, 3) * mm, "end": v(2.54, 2.93) * mm});
            skLineSegment(sketch, "E357", {"start": v(2.54, 2.93) * mm, "end": v(2.51, 2.89) * mm});
            skLineSegment(sketch, "E358", {"start": v(2.51, 2.89) * mm, "end": v(2.49, 2.84) * mm});
            skLineSegment(sketch, "E359", {"start": v(2.49, 2.84) * mm, "end": v(2.47, 2.8) * mm});
            skLineSegment(sketch, "E360", {"start": v(2.47, 2.8) * mm, "end": v(2.45, 2.75) * mm});
            skLineSegment(sketch, "E361", {"start": v(2.45, 2.75) * mm, "end": v(2.45, 2.72) * mm});
            skLineSegment(sketch, "E362", {"start": v(2.45, 2.72) * mm, "end": v(2.45, 2.7) * mm});
            skLineSegment(sketch, "E363", {"start": v(2.45, 2.7) * mm, "end": v(2.45, 2.66) * mm});
            skLineSegment(sketch, "E364", {"start": v(2.45, 2.66) * mm, "end": v(2.45, 2.62) * mm});
            skLineSegment(sketch, "E365", {"start": v(2.45, 2.62) * mm, "end": v(2.5, 2.55) * mm});
            skLineSegment(sketch, "E366", {"start": v(2.5, 2.55) * mm, "end": v(2.73, 2.3) * mm});
            skLineSegment(sketch, "E367", {"start": v(2.73, 2.3) * mm, "end": v(2.95, 2.03) * mm});
            skLineSegment(sketch, "E368", {"start": v(2.95, 2.03) * mm, "end": v(3.01, 1.98) * mm});
            skLineSegment(sketch, "E369", {"start": v(3.01, 1.98) * mm, "end": v(3.05, 1.97) * mm});
            skLineSegment(sketch, "E370", {"start": v(3.05, 1.97) * mm, "end": v(3.08, 1.96) * mm});
            skLineSegment(sketch, "E371", {"start": v(3.08, 1.96) * mm, "end": v(3.1, 1.96) * mm});
            skLineSegment(sketch, "E372", {"start": v(3.1, 1.96) * mm, "end": v(3.13, 1.96) * mm});
            skLineSegment(sketch, "E373", {"start": v(3.13, 1.96) * mm, "end": v(3.19, 1.97) * mm});
            skLineSegment(sketch, "E374", {"start": v(3.19, 1.97) * mm, "end": v(3.23, 1.98) * mm});
            skLineSegment(sketch, "E375", {"start": v(3.23, 1.98) * mm, "end": v(3.28, 2) * mm});
            skLineSegment(sketch, "E376", {"start": v(3.28, 2) * mm, "end": v(3.32, 2.01) * mm});
            skLineSegment(sketch, "E377", {"start": v(3.32, 2.01) * mm, "end": v(3.4, 2.06) * mm});
            skLineSegment(sketch, "E378", {"start": v(3.4, 2.06) * mm, "end": v(3.49, 2.1) * mm});
            skLineSegment(sketch, "E379", {"start": v(3.49, 2.1) * mm, "end": v(3.58, 2.14) * mm});
            skLineSegment(sketch, "E380", {"start": v(3.58, 2.14) * mm, "end": v(3.67, 2.16) * mm});
            skLineSegment(sketch, "E381", {"start": v(3.67, 2.16) * mm, "end": v(3.77, 2.18) * mm});
            skLineSegment(sketch, "E382", {"start": v(3.77, 2.18) * mm, "end": v(3.88, 2.19) * mm});
            skLineSegment(sketch, "E383", {"start": v(3.88, 2.19) * mm, "end": v(3.98, 2.2) * mm});
            skLineSegment(sketch, "E384", {"start": v(3.98, 2.2) * mm, "end": v(4.09, 2.2) * mm});
            skLineSegment(sketch, "E385", {"start": v(4.09, 2.2) * mm, "end": v(4.2, 2.2) * mm});
            skLineSegment(sketch, "E386", {"start": v(4.2, 2.2) * mm, "end": v(4.31, 2.18) * mm});
            skLineSegment(sketch, "E387", {"start": v(4.31, 2.18) * mm, "end": v(4.42, 2.17) * mm});
            skLineSegment(sketch, "E388", {"start": v(4.42, 2.17) * mm, "end": v(4.5, 2.15) * mm});
            skLineSegment(sketch, "E389", {"start": v(4.5, 2.15) * mm, "end": v(4.68, 1.76) * mm});
            skLineSegment(sketch, "E390", {"start": v(4.68, 1.76) * mm, "end": v(4.81, 1.35) * mm});
            skLineSegment(sketch, "E391", {"start": v(4.81, 1.35) * mm, "end": v(4.76, 1.28) * mm});
            skLineSegment(sketch, "E392", {"start": v(4.76, 1.28) * mm, "end": v(4.69, 1.2) * mm});
            skLineSegment(sketch, "E393", {"start": v(4.69, 1.2) * mm, "end": v(4.6, 1.11) * mm});
            skLineSegment(sketch, "E394", {"start": v(4.6, 1.11) * mm, "end": v(4.53, 1.03) * mm});
            skLineSegment(sketch, "E395", {"start": v(4.53, 1.03) * mm, "end": v(4.45, 0.96) * mm});
            skLineSegment(sketch, "E396", {"start": v(4.45, 0.96) * mm, "end": v(4.37, 0.9) * mm});
            skLineSegment(sketch, "E397", {"start": v(4.37, 0.9) * mm, "end": v(4.28, 0.84) * mm});
            skLineSegment(sketch, "E398", {"start": v(4.28, 0.84) * mm, "end": v(4.2, 0.78) * mm});
            skLineSegment(sketch, "E399", {"start": v(4.2, 0.78) * mm, "end": v(4.11, 0.74) * mm});
            skLineSegment(sketch, "E400", {"start": v(4.11, 0.74) * mm, "end": v(4.02, 0.7) * mm});
            skLineSegment(sketch, "E401", {"start": v(4.02, 0.7) * mm, "end": v(3.93, 0.68) * mm});
            skLineSegment(sketch, "E402", {"start": v(3.93, 0.68) * mm, "end": v(3.84, 0.66) * mm});
            skLineSegment(sketch, "E403", {"start": v(3.84, 0.66) * mm, "end": v(3.8, 0.65) * mm});
            skLineSegment(sketch, "E404", {"start": v(3.8, 0.65) * mm, "end": v(3.75, 0.63) * mm});
            skLineSegment(sketch, "E405", {"start": v(3.75, 0.63) * mm, "end": v(3.7, 0.6) * mm});
            skLineSegment(sketch, "E406", {"start": v(3.7, 0.6) * mm, "end": v(3.66, 0.58) * mm});
            skLineSegment(sketch, "E407", {"start": v(3.66, 0.58) * mm, "end": v(3.64, 0.56) * mm});
            skLineSegment(sketch, "E408", {"start": v(3.64, 0.56) * mm, "end": v(3.62, 0.54) * mm});
            skLineSegment(sketch, "E409", {"start": v(3.62, 0.54) * mm, "end": v(3.6, 0.51) * mm});
            skLineSegment(sketch, "E410", {"start": v(3.6, 0.51) * mm, "end": v(3.58, 0.48) * mm});
            skLineSegment(sketch, "E411", {"start": v(3.58, 0.48) * mm, "end": v(3.57, 0.4) * mm});
            skLineSegment(sketch, "E412", {"start": v(3.57, 0.4) * mm, "end": v(3.59, 0.06) * mm});
            skLineSegment(sketch, "E413", {"start": v(3.59, 0.06) * mm, "end": v(3.58, -0.29) * mm});
            skCircle(sketch, "E414", {"center": v(0, 0) * mm, "radius": 0.85 * mm});
            skSolve(sketch);
        }
        {
            var Q0;
            Q0=makeQuery(id+"F0.imprint","IMPRINT",FACE,{"disambiguationData":[TD([[makeQuery(id+"F0.imprint","IMPRINT",EDGE,{"derivedFrom":sQuery(id+"F0.wireOp",EDGE,"E0")}),-1.0]])]});
            extrude(context, id + "F1", {"entities" : qUnion([Q0]), "depth" : 4 * mm});
        }
        {
            var Q0;
            Q0=qCreatedBy(makeId("Front.planeOp"),FACE);
            var sketch = newSketch(context, id + "F2", { "sketchPlane" : qUnion([Q0])});
            skLineSegment(sketch, "E415", {"start": v(-6.64, -0.83) * mm, "end": v(-6.68, -0.75) * mm});
            skLineSegment(sketch, "E416", {"start": v(-6.68, -0.75) * mm, "end": v(-6.71, -0.72) * mm});
            skLineSegment(sketch, "E417", {"start": v(-6.71, -0.72) * mm, "end": v(-6.75, -0.7) * mm});
            skLineSegment(sketch, "E418", {"start": v(-6.75, -0.7) * mm, "end": v(-6.81, -0.67) * mm});
            skLineSegment(sketch, "E419", {"start": v(-6.81, -0.67) * mm, "end": v(-6.87, -0.65) * mm});
            skLineSegment(sketch, "E420", {"start": v(-6.87, -0.65) * mm, "end": v(-6.94, -0.65) * mm});
            skLineSegment(sketch, "E421", {"start": v(-6.94, -0.65) * mm, "end": v(-7.06, -0.63) * mm});
            skLineSegment(sketch, "E422", {"start": v(-7.06, -0.63) * mm, "end": v(-7.18, -0.6) * mm});
            skLineSegment(sketch, "E423", {"start": v(-7.18, -0.6) * mm, "end": v(-7.3, -0.58) * mm});
            skLineSegment(sketch, "E424", {"start": v(-7.3, -0.58) * mm, "end": v(-7.44, -0.54) * mm});
            skLineSegment(sketch, "E425", {"start": v(-7.44, -0.54) * mm, "end": v(-7.56, -0.5) * mm});
            skLineSegment(sketch, "E426", {"start": v(-7.56, -0.5) * mm, "end": v(-7.69, -0.44) * mm});
            skLineSegment(sketch, "E427", {"start": v(-7.69, -0.44) * mm, "end": v(-7.81, -0.38) * mm});
            skLineSegment(sketch, "E428", {"start": v(-7.81, -0.38) * mm, "end": v(-7.9, -0.33) * mm});
            skLineSegment(sketch, "E429", {"start": v(-7.9, -0.33) * mm, "end": v(-7.9, 0.44) * mm});
            skLineSegment(sketch, "E430", {"start": v(-7.9, 0.44) * mm, "end": v(-7.8, 0.49) * mm});
            skLineSegment(sketch, "E431", {"start": v(-7.8, 0.49) * mm, "end": v(-7.68, 0.55) * mm});
            skLineSegment(sketch, "E432", {"start": v(-7.68, 0.55) * mm, "end": v(-7.55, 0.6) * mm});
            skLineSegment(sketch, "E433", {"start": v(-7.55, 0.6) * mm, "end": v(-7.43, 0.64) * mm});
            skLineSegment(sketch, "E434", {"start": v(-7.43, 0.64) * mm, "end": v(-7.3, 0.68) * mm});
            skLineSegment(sketch, "E435", {"start": v(-7.3, 0.68) * mm, "end": v(-7.18, 0.7) * mm});
            skLineSegment(sketch, "E436", {"start": v(-7.18, 0.7) * mm, "end": v(-7.05, 0.73) * mm});
            skLineSegment(sketch, "E437", {"start": v(-7.05, 0.73) * mm, "end": v(-6.93, 0.75) * mm});
            skLineSegment(sketch, "E438", {"start": v(-6.93, 0.75) * mm, "end": v(-6.86, 0.75) * mm});
            skLineSegment(sketch, "E439", {"start": v(-6.86, 0.75) * mm, "end": v(-6.8, 0.77) * mm});
            skLineSegment(sketch, "E440", {"start": v(-6.8, 0.77) * mm, "end": v(-6.74, 0.8) * mm});
            skLineSegment(sketch, "E441", {"start": v(-6.74, 0.8) * mm, "end": v(-6.7, 0.81) * mm});
            skLineSegment(sketch, "E442", {"start": v(-6.7, 0.81) * mm, "end": v(-6.67, 0.84) * mm});
            skLineSegment(sketch, "E443", {"start": v(-6.67, 0.84) * mm, "end": v(-6.63, 0.92) * mm});
            skLineSegment(sketch, "E444", {"start": v(-6.63, 0.92) * mm, "end": v(-6.52, 1.5) * mm});
            skLineSegment(sketch, "E445", {"start": v(-6.52, 1.5) * mm, "end": v(-6.53, 1.58) * mm});
            skLineSegment(sketch, "E446", {"start": v(-6.53, 1.58) * mm, "end": v(-6.55, 1.62) * mm});
            skLineSegment(sketch, "E447", {"start": v(-6.55, 1.62) * mm, "end": v(-6.58, 1.65) * mm});
            skLineSegment(sketch, "E448", {"start": v(-6.58, 1.65) * mm, "end": v(-6.63, 1.7) * mm});
            skLineSegment(sketch, "E449", {"start": v(-6.63, 1.7) * mm, "end": v(-6.68, 1.74) * mm});
            skLineSegment(sketch, "E450", {"start": v(-6.68, 1.74) * mm, "end": v(-6.74, 1.76) * mm});
            skLineSegment(sketch, "E451", {"start": v(-6.74, 1.76) * mm, "end": v(-6.85, 1.82) * mm});
            skLineSegment(sketch, "E452", {"start": v(-6.85, 1.82) * mm, "end": v(-6.96, 1.88) * mm});
            skLineSegment(sketch, "E453", {"start": v(-6.96, 1.88) * mm, "end": v(-7.07, 1.96) * mm});
            skLineSegment(sketch, "E454", {"start": v(-7.07, 1.96) * mm, "end": v(-7.17, 2.04) * mm});
            skLineSegment(sketch, "E455", {"start": v(-7.17, 2.04) * mm, "end": v(-7.27, 2.12) * mm});
            skLineSegment(sketch, "E456", {"start": v(-7.27, 2.12) * mm, "end": v(-7.37, 2.22) * mm});
            skLineSegment(sketch, "E457", {"start": v(-7.37, 2.22) * mm, "end": v(-7.47, 2.31) * mm});
            skLineSegment(sketch, "E458", {"start": v(-7.47, 2.31) * mm, "end": v(-7.54, 2.4) * mm});
            skLineSegment(sketch, "E459", {"start": v(-7.54, 2.4) * mm, "end": v(-7.27, 3.12) * mm});
            skLineSegment(sketch, "E460", {"start": v(-7.27, 3.12) * mm, "end": v(-7.17, 3.13) * mm});
            skLineSegment(sketch, "E461", {"start": v(-7.17, 3.13) * mm, "end": v(-7.03, 3.14) * mm});
            skLineSegment(sketch, "E462", {"start": v(-7.03, 3.14) * mm, "end": v(-6.9, 3.14) * mm});
            skLineSegment(sketch, "E463", {"start": v(-6.9, 3.14) * mm, "end": v(-6.76, 3.14) * mm});
            skLineSegment(sketch, "E464", {"start": v(-6.76, 3.14) * mm, "end": v(-6.63, 3.13) * mm});
            skLineSegment(sketch, "E465", {"start": v(-6.63, 3.13) * mm, "end": v(-6.5, 3.12) * mm});
            skLineSegment(sketch, "E466", {"start": v(-6.5, 3.12) * mm, "end": v(-6.37, 3.1) * mm});
            skLineSegment(sketch, "E467", {"start": v(-6.37, 3.1) * mm, "end": v(-6.25, 3.07) * mm});
            skLineSegment(sketch, "E468", {"start": v(-6.25, 3.07) * mm, "end": v(-6.2, 3.05) * mm});
            skLineSegment(sketch, "E469", {"start": v(-6.2, 3.05) * mm, "end": v(-6.13, 3.05) * mm});
            skLineSegment(sketch, "E470", {"start": v(-6.13, 3.05) * mm, "end": v(-6.06, 3.05) * mm});
            skLineSegment(sketch, "E471", {"start": v(-6.06, 3.05) * mm, "end": v(-6.02, 3.06) * mm});
            skLineSegment(sketch, "E472", {"start": v(-6.02, 3.06) * mm, "end": v(-5.98, 3.07) * mm});
            skLineSegment(sketch, "E473", {"start": v(-5.98, 3.07) * mm, "end": v(-5.91, 3.13) * mm});
            skLineSegment(sketch, "E474", {"start": v(-5.91, 3.13) * mm, "end": v(-5.62, 3.63) * mm});
            skLineSegment(sketch, "E475", {"start": v(-5.62, 3.63) * mm, "end": v(-5.6, 3.72) * mm});
            skLineSegment(sketch, "E476", {"start": v(-5.6, 3.72) * mm, "end": v(-5.6, 3.77) * mm});
            skLineSegment(sketch, "E477", {"start": v(-5.6, 3.77) * mm, "end": v(-5.62, 3.8) * mm});
            skLineSegment(sketch, "E478", {"start": v(-5.62, 3.8) * mm, "end": v(-5.65, 3.86) * mm});
            skLineSegment(sketch, "E479", {"start": v(-5.65, 3.86) * mm, "end": v(-5.69, 3.92) * mm});
            skLineSegment(sketch, "E480", {"start": v(-5.69, 3.92) * mm, "end": v(-5.73, 3.96) * mm});
            skLineSegment(sketch, "E481", {"start": v(-5.73, 3.96) * mm, "end": v(-5.82, 4.05) * mm});
            skLineSegment(sketch, "E482", {"start": v(-5.82, 4.05) * mm, "end": v(-5.9, 4.15) * mm});
            skLineSegment(sketch, "E483", {"start": v(-5.9, 4.15) * mm, "end": v(-5.97, 4.26) * mm});
            skLineSegment(sketch, "E484", {"start": v(-5.97, 4.26) * mm, "end": v(-6.04, 4.37) * mm});
            skLineSegment(sketch, "E485", {"start": v(-6.04, 4.37) * mm, "end": v(-6.1, 4.48) * mm});
            skLineSegment(sketch, "E486", {"start": v(-6.1, 4.48) * mm, "end": v(-6.17, 4.6) * mm});
            skLineSegment(sketch, "E487", {"start": v(-6.17, 4.6) * mm, "end": v(-6.23, 4.73) * mm});
            skLineSegment(sketch, "E488", {"start": v(-6.23, 4.73) * mm, "end": v(-6.27, 4.83) * mm});
            skLineSegment(sketch, "E489", {"start": v(-6.27, 4.83) * mm, "end": v(-5.77, 5.42) * mm});
            skLineSegment(sketch, "E490", {"start": v(-5.77, 5.42) * mm, "end": v(-5.67, 5.4) * mm});
            skLineSegment(sketch, "E491", {"start": v(-5.67, 5.4) * mm, "end": v(-5.53, 5.35) * mm});
            skLineSegment(sketch, "E492", {"start": v(-5.53, 5.35) * mm, "end": v(-5.4, 5.31) * mm});
            skLineSegment(sketch, "E493", {"start": v(-5.4, 5.31) * mm, "end": v(-5.28, 5.27) * mm});
            skLineSegment(sketch, "E494", {"start": v(-5.28, 5.27) * mm, "end": v(-5.16, 5.21) * mm});
            skLineSegment(sketch, "E495", {"start": v(-5.16, 5.21) * mm, "end": v(-5.04, 5.16) * mm});
            skLineSegment(sketch, "E496", {"start": v(-5.04, 5.16) * mm, "end": v(-4.93, 5.1) * mm});
            skLineSegment(sketch, "E497", {"start": v(-4.93, 5.1) * mm, "end": v(-4.83, 5.02) * mm});
            skLineSegment(sketch, "E498", {"start": v(-4.83, 5.02) * mm, "end": v(-4.78, 4.99) * mm});
            skLineSegment(sketch, "E499", {"start": v(-4.78, 4.99) * mm, "end": v(-4.72, 4.96) * mm});
            skLineSegment(sketch, "E500", {"start": v(-4.72, 4.96) * mm, "end": v(-4.65, 4.94) * mm});
            skLineSegment(sketch, "E501", {"start": v(-4.65, 4.94) * mm, "end": v(-4.61, 4.93) * mm});
            skLineSegment(sketch, "E502", {"start": v(-4.61, 4.93) * mm, "end": v(-4.57, 4.93) * mm});
            skLineSegment(sketch, "E503", {"start": v(-4.57, 4.93) * mm, "end": v(-4.49, 4.96) * mm});
            skLineSegment(sketch, "E504", {"start": v(-4.49, 4.96) * mm, "end": v(-4.04, 5.34) * mm});
            skLineSegment(sketch, "E505", {"start": v(-4.04, 5.34) * mm, "end": v(-3.99, 5.41) * mm});
            skLineSegment(sketch, "E506", {"start": v(-3.99, 5.41) * mm, "end": v(-3.98, 5.46) * mm});
            skLineSegment(sketch, "E507", {"start": v(-3.98, 5.46) * mm, "end": v(-3.98, 5.5) * mm});
            skLineSegment(sketch, "E508", {"start": v(-3.98, 5.5) * mm, "end": v(-3.99, 5.56) * mm});
            skLineSegment(sketch, "E509", {"start": v(-3.99, 5.56) * mm, "end": v(-4, 5.63) * mm});
            skLineSegment(sketch, "E510", {"start": v(-4, 5.63) * mm, "end": v(-4.03, 5.68) * mm});
            skLineSegment(sketch, "E511", {"start": v(-4.03, 5.68) * mm, "end": v(-4.08, 5.8) * mm});
            skLineSegment(sketch, "E512", {"start": v(-4.08, 5.8) * mm, "end": v(-4.12, 5.92) * mm});
            skLineSegment(sketch, "E513", {"start": v(-4.12, 5.92) * mm, "end": v(-4.15, 6.04) * mm});
            skLineSegment(sketch, "E514", {"start": v(-4.15, 6.04) * mm, "end": v(-4.18, 6.17) * mm});
            skLineSegment(sketch, "E515", {"start": v(-4.18, 6.17) * mm, "end": v(-4.2, 6.3) * mm});
            skLineSegment(sketch, "E516", {"start": v(-4.2, 6.3) * mm, "end": v(-4.22, 6.44) * mm});
            skLineSegment(sketch, "E517", {"start": v(-4.22, 6.44) * mm, "end": v(-4.24, 6.58) * mm});
            skLineSegment(sketch, "E518", {"start": v(-4.24, 6.58) * mm, "end": v(-4.24, 6.68) * mm});
            skLineSegment(sketch, "E519", {"start": v(-4.24, 6.68) * mm, "end": v(-3.57, 7.06) * mm});
            skLineSegment(sketch, "E520", {"start": v(-3.57, 7.06) * mm, "end": v(-3.48, 7) * mm});
            skLineSegment(sketch, "E521", {"start": v(-3.48, 7) * mm, "end": v(-3.37, 6.92) * mm});
            skLineSegment(sketch, "E522", {"start": v(-3.37, 6.92) * mm, "end": v(-3.26, 6.84) * mm});
            skLineSegment(sketch, "E523", {"start": v(-3.26, 6.84) * mm, "end": v(-3.16, 6.75) * mm});
            skLineSegment(sketch, "E524", {"start": v(-3.16, 6.75) * mm, "end": v(-3.06, 6.66) * mm});
            skLineSegment(sketch, "E525", {"start": v(-3.06, 6.66) * mm, "end": v(-2.97, 6.57) * mm});
            skLineSegment(sketch, "E526", {"start": v(-2.97, 6.57) * mm, "end": v(-2.9, 6.47) * mm});
            skLineSegment(sketch, "E527", {"start": v(-2.9, 6.47) * mm, "end": v(-2.82, 6.37) * mm});
            skLineSegment(sketch, "E528", {"start": v(-2.82, 6.37) * mm, "end": v(-2.78, 6.32) * mm});
            skLineSegment(sketch, "E529", {"start": v(-2.78, 6.32) * mm, "end": v(-2.73, 6.27) * mm});
            skLineSegment(sketch, "E530", {"start": v(-2.73, 6.27) * mm, "end": v(-2.68, 6.23) * mm});
            skLineSegment(sketch, "E531", {"start": v(-2.68, 6.23) * mm, "end": v(-2.65, 6.21) * mm});
            skLineSegment(sketch, "E532", {"start": v(-2.65, 6.21) * mm, "end": v(-2.6, 6.2) * mm});
            skLineSegment(sketch, "E533", {"start": v(-2.6, 6.2) * mm, "end": v(-2.52, 6.2) * mm});
            skLineSegment(sketch, "E534", {"start": v(-2.52, 6.2) * mm, "end": v(-1.97, 6.4) * mm});
            skLineSegment(sketch, "E535", {"start": v(-1.97, 6.4) * mm, "end": v(-1.9, 6.45) * mm});
            skLineSegment(sketch, "E536", {"start": v(-1.9, 6.45) * mm, "end": v(-1.87, 6.49) * mm});
            skLineSegment(sketch, "E537", {"start": v(-1.87, 6.49) * mm, "end": v(-1.86, 6.52) * mm});
            skLineSegment(sketch, "E538", {"start": v(-1.86, 6.52) * mm, "end": v(-1.85, 6.59) * mm});
            skLineSegment(sketch, "E539", {"start": v(-1.85, 6.59) * mm, "end": v(-1.84, 6.66) * mm});
            skLineSegment(sketch, "E540", {"start": v(-1.84, 6.66) * mm, "end": v(-1.84, 6.72) * mm});
            skLineSegment(sketch, "E541", {"start": v(-1.84, 6.72) * mm, "end": v(-1.85, 6.84) * mm});
            skLineSegment(sketch, "E542", {"start": v(-1.85, 6.84) * mm, "end": v(-1.85, 6.97) * mm});
            skLineSegment(sketch, "E543", {"start": v(-1.85, 6.97) * mm, "end": v(-1.84, 7.1) * mm});
            skLineSegment(sketch, "E544", {"start": v(-1.84, 7.1) * mm, "end": v(-1.82, 7.23) * mm});
            skLineSegment(sketch, "E545", {"start": v(-1.82, 7.23) * mm, "end": v(-1.8, 7.36) * mm});
            skLineSegment(sketch, "E546", {"start": v(-1.8, 7.36) * mm, "end": v(-1.77, 7.5) * mm});
            skLineSegment(sketch, "E547", {"start": v(-1.77, 7.5) * mm, "end": v(-1.73, 7.63) * mm});
            skLineSegment(sketch, "E548", {"start": v(-1.73, 7.63) * mm, "end": v(-1.7, 7.73) * mm});
            skLineSegment(sketch, "E549", {"start": v(-1.7, 7.73) * mm, "end": v(-0.94, 7.86) * mm});
            skLineSegment(sketch, "E550", {"start": v(-0.94, 7.86) * mm, "end": v(-0.87, 7.77) * mm});
            skLineSegment(sketch, "E551", {"start": v(-0.87, 7.77) * mm, "end": v(-0.8, 7.66) * mm});
            skLineSegment(sketch, "E552", {"start": v(-0.8, 7.66) * mm, "end": v(-0.72, 7.54) * mm});
            skLineSegment(sketch, "E553", {"start": v(-0.72, 7.54) * mm, "end": v(-0.66, 7.43) * mm});
            skLineSegment(sketch, "E554", {"start": v(-0.66, 7.43) * mm, "end": v(-0.6, 7.3) * mm});
            skLineSegment(sketch, "E555", {"start": v(-0.6, 7.3) * mm, "end": v(-0.55, 7.19) * mm});
            skLineSegment(sketch, "E556", {"start": v(-0.55, 7.19) * mm, "end": v(-0.5, 7.07) * mm});
            skLineSegment(sketch, "E557", {"start": v(-0.5, 7.07) * mm, "end": v(-0.47, 6.95) * mm});
            skLineSegment(sketch, "E558", {"start": v(-0.47, 6.95) * mm, "end": v(-0.45, 6.89) * mm});
            skLineSegment(sketch, "E559", {"start": v(-0.45, 6.89) * mm, "end": v(-0.42, 6.83) * mm});
            skLineSegment(sketch, "E560", {"start": v(-0.42, 6.83) * mm, "end": v(-0.39, 6.77) * mm});
            skLineSegment(sketch, "E561", {"start": v(-0.39, 6.77) * mm, "end": v(-0.36, 6.74) * mm});
            skLineSegment(sketch, "E562", {"start": v(-0.36, 6.74) * mm, "end": v(-0.33, 6.71) * mm});
            skLineSegment(sketch, "E563", {"start": v(-0.33, 6.71) * mm, "end": v(-0.25, 6.69) * mm});
            skLineSegment(sketch, "E564", {"start": v(-0.25, 6.69) * mm, "end": v(0.34, 6.68) * mm});
            skLineSegment(sketch, "E565", {"start": v(0.34, 6.68) * mm, "end": v(0.42, 6.7) * mm});
            skLineSegment(sketch, "E566", {"start": v(0.42, 6.7) * mm, "end": v(0.46, 6.74) * mm});
            skLineSegment(sketch, "E567", {"start": v(0.46, 6.74) * mm, "end": v(0.48, 6.77) * mm});
            skLineSegment(sketch, "E568", {"start": v(0.48, 6.77) * mm, "end": v(0.52, 6.82) * mm});
            skLineSegment(sketch, "E569", {"start": v(0.52, 6.82) * mm, "end": v(0.55, 6.88) * mm});
            skLineSegment(sketch, "E570", {"start": v(0.55, 6.88) * mm, "end": v(0.56, 6.94) * mm});
            skLineSegment(sketch, "E571", {"start": v(0.56, 6.94) * mm, "end": v(0.6, 7.06) * mm});
            skLineSegment(sketch, "E572", {"start": v(0.6, 7.06) * mm, "end": v(0.65, 7.18) * mm});
            skLineSegment(sketch, "E573", {"start": v(0.65, 7.18) * mm, "end": v(0.7, 7.3) * mm});
            skLineSegment(sketch, "E574", {"start": v(0.7, 7.3) * mm, "end": v(0.76, 7.42) * mm});
            skLineSegment(sketch, "E575", {"start": v(0.76, 7.42) * mm, "end": v(0.83, 7.53) * mm});
            skLineSegment(sketch, "E576", {"start": v(0.83, 7.53) * mm, "end": v(0.9, 7.65) * mm});
            skLineSegment(sketch, "E577", {"start": v(0.9, 7.65) * mm, "end": v(0.98, 7.76) * mm});
            skLineSegment(sketch, "E578", {"start": v(0.98, 7.76) * mm, "end": v(1.04, 7.84) * mm});
            skLineSegment(sketch, "E579", {"start": v(1.04, 7.84) * mm, "end": v(1.8, 7.7) * mm});
            skLineSegment(sketch, "E580", {"start": v(1.8, 7.7) * mm, "end": v(1.84, 7.6) * mm});
            skLineSegment(sketch, "E581", {"start": v(1.84, 7.6) * mm, "end": v(1.87, 7.47) * mm});
            skLineSegment(sketch, "E582", {"start": v(1.87, 7.47) * mm, "end": v(1.9, 7.34) * mm});
            skLineSegment(sketch, "E583", {"start": v(1.9, 7.34) * mm, "end": v(1.92, 7.2) * mm});
            skLineSegment(sketch, "E584", {"start": v(1.92, 7.2) * mm, "end": v(1.94, 7.07) * mm});
            skLineSegment(sketch, "E585", {"start": v(1.94, 7.07) * mm, "end": v(1.94, 6.94) * mm});
            skLineSegment(sketch, "E586", {"start": v(1.94, 6.94) * mm, "end": v(1.95, 6.82) * mm});
            skLineSegment(sketch, "E587", {"start": v(1.95, 6.82) * mm, "end": v(1.94, 6.7) * mm});
            skLineSegment(sketch, "E588", {"start": v(1.94, 6.7) * mm, "end": v(1.93, 6.63) * mm});
            skLineSegment(sketch, "E589", {"start": v(1.93, 6.63) * mm, "end": v(1.94, 6.56) * mm});
            skLineSegment(sketch, "E590", {"start": v(1.94, 6.56) * mm, "end": v(1.95, 6.5) * mm});
            skLineSegment(sketch, "E591", {"start": v(1.95, 6.5) * mm, "end": v(1.96, 6.46) * mm});
            skLineSegment(sketch, "E592", {"start": v(1.96, 6.46) * mm, "end": v(1.98, 6.42) * mm});
            skLineSegment(sketch, "E593", {"start": v(1.98, 6.42) * mm, "end": v(2.06, 6.37) * mm});
            skLineSegment(sketch, "E594", {"start": v(2.06, 6.37) * mm, "end": v(2.6, 6.16) * mm});
            skLineSegment(sketch, "E595", {"start": v(2.6, 6.16) * mm, "end": v(2.7, 6.16) * mm});
            skLineSegment(sketch, "E596", {"start": v(2.7, 6.16) * mm, "end": v(2.74, 6.17) * mm});
            skLineSegment(sketch, "E597", {"start": v(2.74, 6.17) * mm, "end": v(2.77, 6.2) * mm});
            skLineSegment(sketch, "E598", {"start": v(2.77, 6.2) * mm, "end": v(2.82, 6.23) * mm});
            skLineSegment(sketch, "E599", {"start": v(2.82, 6.23) * mm, "end": v(2.87, 6.28) * mm});
            skLineSegment(sketch, "E600", {"start": v(2.87, 6.28) * mm, "end": v(2.9, 6.33) * mm});
            skLineSegment(sketch, "E601", {"start": v(2.9, 6.33) * mm, "end": v(2.98, 6.43) * mm});
            skLineSegment(sketch, "E602", {"start": v(2.98, 6.43) * mm, "end": v(3.06, 6.53) * mm});
            skLineSegment(sketch, "E603", {"start": v(3.06, 6.53) * mm, "end": v(3.16, 6.62) * mm});
            skLineSegment(sketch, "E604", {"start": v(3.16, 6.62) * mm, "end": v(3.25, 6.7) * mm});
            skLineSegment(sketch, "E605", {"start": v(3.25, 6.7) * mm, "end": v(3.36, 6.8) * mm});
            skLineSegment(sketch, "E606", {"start": v(3.36, 6.8) * mm, "end": v(3.46, 6.88) * mm});
            skLineSegment(sketch, "E607", {"start": v(3.46, 6.88) * mm, "end": v(3.58, 6.96) * mm});
            skLineSegment(sketch, "E608", {"start": v(3.58, 6.96) * mm, "end": v(3.66, 7.01) * mm});
            skLineSegment(sketch, "E609", {"start": v(3.66, 7.01) * mm, "end": v(4.33, 6.62) * mm});
            skLineSegment(sketch, "E610", {"start": v(4.33, 6.62) * mm, "end": v(4.33, 6.52) * mm});
            skLineSegment(sketch, "E611", {"start": v(4.33, 6.52) * mm, "end": v(4.31, 6.38) * mm});
            skLineSegment(sketch, "E612", {"start": v(4.31, 6.38) * mm, "end": v(4.3, 6.24) * mm});
            skLineSegment(sketch, "E613", {"start": v(4.3, 6.24) * mm, "end": v(4.27, 6.11) * mm});
            skLineSegment(sketch, "E614", {"start": v(4.27, 6.11) * mm, "end": v(4.24, 5.98) * mm});
            skLineSegment(sketch, "E615", {"start": v(4.24, 5.98) * mm, "end": v(4.2, 5.86) * mm});
            skLineSegment(sketch, "E616", {"start": v(4.2, 5.86) * mm, "end": v(4.16, 5.74) * mm});
            skLineSegment(sketch, "E617", {"start": v(4.16, 5.74) * mm, "end": v(4.1, 5.62) * mm});
            skLineSegment(sketch, "E618", {"start": v(4.1, 5.62) * mm, "end": v(4.08, 5.57) * mm});
            skLineSegment(sketch, "E619", {"start": v(4.08, 5.57) * mm, "end": v(4.07, 5.5) * mm});
            skLineSegment(sketch, "E620", {"start": v(4.07, 5.5) * mm, "end": v(4.05, 5.44) * mm});
            skLineSegment(sketch, "E621", {"start": v(4.05, 5.44) * mm, "end": v(4.05, 5.4) * mm});
            skLineSegment(sketch, "E622", {"start": v(4.05, 5.4) * mm, "end": v(4.06, 5.36) * mm});
            skLineSegment(sketch, "E623", {"start": v(4.06, 5.36) * mm, "end": v(4.1, 5.28) * mm});
            skLineSegment(sketch, "E624", {"start": v(4.1, 5.28) * mm, "end": v(4.55, 4.9) * mm});
            skLineSegment(sketch, "E625", {"start": v(4.55, 4.9) * mm, "end": v(4.64, 4.87) * mm});
            skLineSegment(sketch, "E626", {"start": v(4.64, 4.87) * mm, "end": v(4.68, 4.87) * mm});
            skLineSegment(sketch, "E627", {"start": v(4.68, 4.87) * mm, "end": v(4.72, 4.87) * mm});
            skLineSegment(sketch, "E628", {"start": v(4.72, 4.87) * mm, "end": v(4.78, 4.9) * mm});
            skLineSegment(sketch, "E629", {"start": v(4.78, 4.9) * mm, "end": v(4.85, 4.92) * mm});
            skLineSegment(sketch, "E630", {"start": v(4.85, 4.92) * mm, "end": v(4.9, 4.96) * mm});
            skLineSegment(sketch, "E631", {"start": v(4.9, 4.96) * mm, "end": v(5, 5.02) * mm});
            skLineSegment(sketch, "E632", {"start": v(5, 5.02) * mm, "end": v(5.11, 5.09) * mm});
            skLineSegment(sketch, "E633", {"start": v(5.11, 5.09) * mm, "end": v(5.23, 5.14) * mm});
            skLineSegment(sketch, "E634", {"start": v(5.23, 5.14) * mm, "end": v(5.35, 5.2) * mm});
            skLineSegment(sketch, "E635", {"start": v(5.35, 5.2) * mm, "end": v(5.48, 5.24) * mm});
            skLineSegment(sketch, "E636", {"start": v(5.48, 5.24) * mm, "end": v(5.6, 5.28) * mm});
            skLineSegment(sketch, "E637", {"start": v(5.6, 5.28) * mm, "end": v(5.74, 5.31) * mm});
            skLineSegment(sketch, "E638", {"start": v(5.74, 5.31) * mm, "end": v(5.84, 5.34) * mm});
            skLineSegment(sketch, "E639", {"start": v(5.84, 5.34) * mm, "end": v(6.34, 4.74) * mm});
            skLineSegment(sketch, "E640", {"start": v(6.34, 4.74) * mm, "end": v(6.3, 4.64) * mm});
            skLineSegment(sketch, "E641", {"start": v(6.3, 4.64) * mm, "end": v(6.23, 4.52) * mm});
            skLineSegment(sketch, "E642", {"start": v(6.23, 4.52) * mm, "end": v(6.17, 4.4) * mm});
            skLineSegment(sketch, "E643", {"start": v(6.17, 4.4) * mm, "end": v(6.1, 4.28) * mm});
            skLineSegment(sketch, "E644", {"start": v(6.1, 4.28) * mm, "end": v(6.03, 4.17) * mm});
            skLineSegment(sketch, "E645", {"start": v(6.03, 4.17) * mm, "end": v(5.95, 4.07) * mm});
            skLineSegment(sketch, "E646", {"start": v(5.95, 4.07) * mm, "end": v(5.87, 3.97) * mm});
            skLineSegment(sketch, "E647", {"start": v(5.87, 3.97) * mm, "end": v(5.79, 3.88) * mm});
            skLineSegment(sketch, "E648", {"start": v(5.79, 3.88) * mm, "end": v(5.74, 3.84) * mm});
            skLineSegment(sketch, "E649", {"start": v(5.74, 3.84) * mm, "end": v(5.7, 3.78) * mm});
            skLineSegment(sketch, "E650", {"start": v(5.7, 3.78) * mm, "end": v(5.67, 3.72) * mm});
            skLineSegment(sketch, "E651", {"start": v(5.67, 3.72) * mm, "end": v(5.66, 3.69) * mm});
            skLineSegment(sketch, "E652", {"start": v(5.66, 3.69) * mm, "end": v(5.65, 3.64) * mm});
            skLineSegment(sketch, "E653", {"start": v(5.65, 3.64) * mm, "end": v(5.67, 3.56) * mm});
            skLineSegment(sketch, "E654", {"start": v(5.67, 3.56) * mm, "end": v(5.96, 3.05) * mm});
            skLineSegment(sketch, "E655", {"start": v(5.96, 3.05) * mm, "end": v(6.02, 2.99) * mm});
            skLineSegment(sketch, "E656", {"start": v(6.02, 2.99) * mm, "end": v(6.06, 2.97) * mm});
            skLineSegment(sketch, "E657", {"start": v(6.06, 2.97) * mm, "end": v(6.1, 2.96) * mm});
            skLineSegment(sketch, "E658", {"start": v(6.1, 2.96) * mm, "end": v(6.17, 2.96) * mm});
            skLineSegment(sketch, "E659", {"start": v(6.17, 2.96) * mm, "end": v(6.24, 2.96) * mm});
            skLineSegment(sketch, "E660", {"start": v(6.24, 2.96) * mm, "end": v(6.3, 2.98) * mm});
            skLineSegment(sketch, "E661", {"start": v(6.3, 2.98) * mm, "end": v(6.42, 3.01) * mm});
            skLineSegment(sketch, "E662", {"start": v(6.42, 3.01) * mm, "end": v(6.54, 3.03) * mm});
            skLineSegment(sketch, "E663", {"start": v(6.54, 3.03) * mm, "end": v(6.67, 3.04) * mm});
            skLineSegment(sketch, "E664", {"start": v(6.67, 3.04) * mm, "end": v(6.8, 3.05) * mm});
            skLineSegment(sketch, "E665", {"start": v(6.8, 3.05) * mm, "end": v(6.94, 3.05) * mm});
            skLineSegment(sketch, "E666", {"start": v(6.94, 3.05) * mm, "end": v(7.07, 3.04) * mm});
            skLineSegment(sketch, "E667", {"start": v(7.07, 3.04) * mm, "end": v(7.21, 3.03) * mm});
            skLineSegment(sketch, "E668", {"start": v(7.21, 3.03) * mm, "end": v(7.32, 3.02) * mm});
            skLineSegment(sketch, "E669", {"start": v(7.32, 3.02) * mm, "end": v(7.58, 2.29) * mm});
            skLineSegment(sketch, "E670", {"start": v(7.58, 2.29) * mm, "end": v(7.5, 2.2) * mm});
            skLineSegment(sketch, "E671", {"start": v(7.5, 2.2) * mm, "end": v(7.4, 2.11) * mm});
            skLineSegment(sketch, "E672", {"start": v(7.4, 2.11) * mm, "end": v(7.3, 2.02) * mm});
            skLineSegment(sketch, "E673", {"start": v(7.3, 2.02) * mm, "end": v(7.2, 1.94) * mm});
            skLineSegment(sketch, "E674", {"start": v(7.2, 1.94) * mm, "end": v(7.1, 1.86) * mm});
            skLineSegment(sketch, "E675", {"start": v(7.1, 1.86) * mm, "end": v(6.99, 1.79) * mm});
            skLineSegment(sketch, "E676", {"start": v(6.99, 1.79) * mm, "end": v(6.88, 1.72) * mm});
            skLineSegment(sketch, "E677", {"start": v(6.88, 1.72) * mm, "end": v(6.76, 1.67) * mm});
            skLineSegment(sketch, "E678", {"start": v(6.76, 1.67) * mm, "end": v(6.7, 1.64) * mm});
            skLineSegment(sketch, "E679", {"start": v(6.7, 1.64) * mm, "end": v(6.65, 1.6) * mm});
            skLineSegment(sketch, "E680", {"start": v(6.65, 1.6) * mm, "end": v(6.6, 1.56) * mm});
            skLineSegment(sketch, "E681", {"start": v(6.6, 1.56) * mm, "end": v(6.58, 1.53) * mm});
            skLineSegment(sketch, "E682", {"start": v(6.58, 1.53) * mm, "end": v(6.55, 1.5) * mm});
            skLineSegment(sketch, "E683", {"start": v(6.55, 1.5) * mm, "end": v(6.54, 1.4) * mm});
            skLineSegment(sketch, "E684", {"start": v(6.54, 1.4) * mm, "end": v(6.64, 0.83) * mm});
            skLineSegment(sketch, "E685", {"start": v(6.64, 0.83) * mm, "end": v(6.68, 0.75) * mm});
            skLineSegment(sketch, "E686", {"start": v(6.68, 0.75) * mm, "end": v(6.71, 0.72) * mm});
            skLineSegment(sketch, "E687", {"start": v(6.71, 0.72) * mm, "end": v(6.75, 0.7) * mm});
            skLineSegment(sketch, "E688", {"start": v(6.75, 0.7) * mm, "end": v(6.81, 0.67) * mm});
            skLineSegment(sketch, "E689", {"start": v(6.81, 0.67) * mm, "end": v(6.87, 0.65) * mm});
            skLineSegment(sketch, "E690", {"start": v(6.87, 0.65) * mm, "end": v(6.94, 0.65) * mm});
            skLineSegment(sketch, "E691", {"start": v(6.94, 0.65) * mm, "end": v(7.06, 0.63) * mm});
            skLineSegment(sketch, "E692", {"start": v(7.06, 0.63) * mm, "end": v(7.18, 0.6) * mm});
            skLineSegment(sketch, "E693", {"start": v(7.18, 0.6) * mm, "end": v(7.3, 0.58) * mm});
            skLineSegment(sketch, "E694", {"start": v(7.3, 0.58) * mm, "end": v(7.44, 0.54) * mm});
            skLineSegment(sketch, "E695", {"start": v(7.44, 0.54) * mm, "end": v(7.56, 0.5) * mm});
            skLineSegment(sketch, "E696", {"start": v(7.56, 0.5) * mm, "end": v(7.69, 0.44) * mm});
            skLineSegment(sketch, "E697", {"start": v(7.69, 0.44) * mm, "end": v(7.81, 0.38) * mm});
            skLineSegment(sketch, "E698", {"start": v(7.81, 0.38) * mm, "end": v(7.9, 0.33) * mm});
            skLineSegment(sketch, "E699", {"start": v(7.9, 0.33) * mm, "end": v(7.9, -0.44) * mm});
            skLineSegment(sketch, "E700", {"start": v(7.9, -0.44) * mm, "end": v(7.8, -0.49) * mm});
            skLineSegment(sketch, "E701", {"start": v(7.8, -0.49) * mm, "end": v(7.68, -0.55) * mm});
            skLineSegment(sketch, "E702", {"start": v(7.68, -0.55) * mm, "end": v(7.55, -0.6) * mm});
            skLineSegment(sketch, "E703", {"start": v(7.55, -0.6) * mm, "end": v(7.43, -0.64) * mm});
            skLineSegment(sketch, "E704", {"start": v(7.43, -0.64) * mm, "end": v(7.3, -0.68) * mm});
            skLineSegment(sketch, "E705", {"start": v(7.3, -0.68) * mm, "end": v(7.18, -0.7) * mm});
            skLineSegment(sketch, "E706", {"start": v(7.18, -0.7) * mm, "end": v(7.05, -0.73) * mm});
            skLineSegment(sketch, "E707", {"start": v(7.05, -0.73) * mm, "end": v(6.93, -0.75) * mm});
            skLineSegment(sketch, "E708", {"start": v(6.93, -0.75) * mm, "end": v(6.86, -0.75) * mm});
            skLineSegment(sketch, "E709", {"start": v(6.86, -0.75) * mm, "end": v(6.8, -0.77) * mm});
            skLineSegment(sketch, "E710", {"start": v(6.8, -0.77) * mm, "end": v(6.74, -0.8) * mm});
            skLineSegment(sketch, "E711", {"start": v(6.74, -0.8) * mm, "end": v(6.7, -0.81) * mm});
            skLineSegment(sketch, "E712", {"start": v(6.7, -0.81) * mm, "end": v(6.67, -0.84) * mm});
            skLineSegment(sketch, "E713", {"start": v(6.67, -0.84) * mm, "end": v(6.63, -0.92) * mm});
            skLineSegment(sketch, "E714", {"start": v(6.63, -0.92) * mm, "end": v(6.52, -1.5) * mm});
            skLineSegment(sketch, "E715", {"start": v(6.52, -1.5) * mm, "end": v(6.53, -1.58) * mm});
            skLineSegment(sketch, "E716", {"start": v(6.53, -1.58) * mm, "end": v(6.55, -1.62) * mm});
            skLineSegment(sketch, "E717", {"start": v(6.55, -1.62) * mm, "end": v(6.58, -1.65) * mm});
            skLineSegment(sketch, "E718", {"start": v(6.58, -1.65) * mm, "end": v(6.63, -1.7) * mm});
            skLineSegment(sketch, "E719", {"start": v(6.63, -1.7) * mm, "end": v(6.68, -1.74) * mm});
            skLineSegment(sketch, "E720", {"start": v(6.68, -1.74) * mm, "end": v(6.74, -1.76) * mm});
            skLineSegment(sketch, "E721", {"start": v(6.74, -1.76) * mm, "end": v(6.85, -1.82) * mm});
            skLineSegment(sketch, "E722", {"start": v(6.85, -1.82) * mm, "end": v(6.96, -1.88) * mm});
            skLineSegment(sketch, "E723", {"start": v(6.96, -1.88) * mm, "end": v(7.07, -1.96) * mm});
            skLineSegment(sketch, "E724", {"start": v(7.07, -1.96) * mm, "end": v(7.17, -2.04) * mm});
            skLineSegment(sketch, "E725", {"start": v(7.17, -2.04) * mm, "end": v(7.27, -2.12) * mm});
            skLineSegment(sketch, "E726", {"start": v(7.27, -2.12) * mm, "end": v(7.37, -2.22) * mm});
            skLineSegment(sketch, "E727", {"start": v(7.37, -2.22) * mm, "end": v(7.47, -2.31) * mm});
            skLineSegment(sketch, "E728", {"start": v(7.47, -2.31) * mm, "end": v(7.54, -2.4) * mm});
            skLineSegment(sketch, "E729", {"start": v(7.54, -2.4) * mm, "end": v(7.27, -3.12) * mm});
            skLineSegment(sketch, "E730", {"start": v(7.27, -3.12) * mm, "end": v(7.17, -3.13) * mm});
            skLineSegment(sketch, "E731", {"start": v(7.17, -3.13) * mm, "end": v(7.03, -3.14) * mm});
            skLineSegment(sketch, "E732", {"start": v(7.03, -3.14) * mm, "end": v(6.9, -3.14) * mm});
            skLineSegment(sketch, "E733", {"start": v(6.9, -3.14) * mm, "end": v(6.76, -3.14) * mm});
            skLineSegment(sketch, "E734", {"start": v(6.76, -3.14) * mm, "end": v(6.63, -3.13) * mm});
            skLineSegment(sketch, "E735", {"start": v(6.63, -3.13) * mm, "end": v(6.5, -3.12) * mm});
            skLineSegment(sketch, "E736", {"start": v(6.5, -3.12) * mm, "end": v(6.37, -3.1) * mm});
            skLineSegment(sketch, "E737", {"start": v(6.37, -3.1) * mm, "end": v(6.25, -3.07) * mm});
            skLineSegment(sketch, "E738", {"start": v(6.25, -3.07) * mm, "end": v(6.2, -3.05) * mm});
            skLineSegment(sketch, "E739", {"start": v(6.2, -3.05) * mm, "end": v(6.13, -3.05) * mm});
            skLineSegment(sketch, "E740", {"start": v(6.13, -3.05) * mm, "end": v(6.06, -3.05) * mm});
            skLineSegment(sketch, "E741", {"start": v(6.06, -3.05) * mm, "end": v(6.02, -3.06) * mm});
            skLineSegment(sketch, "E742", {"start": v(6.02, -3.06) * mm, "end": v(5.98, -3.07) * mm});
            skLineSegment(sketch, "E743", {"start": v(5.98, -3.07) * mm, "end": v(5.91, -3.13) * mm});
            skLineSegment(sketch, "E744", {"start": v(5.91, -3.13) * mm, "end": v(5.62, -3.63) * mm});
            skLineSegment(sketch, "E745", {"start": v(5.62, -3.63) * mm, "end": v(5.6, -3.72) * mm});
            skLineSegment(sketch, "E746", {"start": v(5.6, -3.72) * mm, "end": v(5.6, -3.77) * mm});
            skLineSegment(sketch, "E747", {"start": v(5.6, -3.77) * mm, "end": v(5.62, -3.8) * mm});
            skLineSegment(sketch, "E748", {"start": v(5.62, -3.8) * mm, "end": v(5.65, -3.86) * mm});
            skLineSegment(sketch, "E749", {"start": v(5.65, -3.86) * mm, "end": v(5.69, -3.92) * mm});
            skLineSegment(sketch, "E750", {"start": v(5.69, -3.92) * mm, "end": v(5.73, -3.96) * mm});
            skLineSegment(sketch, "E751", {"start": v(5.73, -3.96) * mm, "end": v(5.82, -4.05) * mm});
            skLineSegment(sketch, "E752", {"start": v(5.82, -4.05) * mm, "end": v(5.9, -4.15) * mm});
            skLineSegment(sketch, "E753", {"start": v(5.9, -4.15) * mm, "end": v(5.97, -4.26) * mm});
            skLineSegment(sketch, "E754", {"start": v(5.97, -4.26) * mm, "end": v(6.04, -4.37) * mm});
            skLineSegment(sketch, "E755", {"start": v(6.04, -4.37) * mm, "end": v(6.1, -4.48) * mm});
            skLineSegment(sketch, "E756", {"start": v(6.1, -4.48) * mm, "end": v(6.17, -4.6) * mm});
            skLineSegment(sketch, "E757", {"start": v(6.17, -4.6) * mm, "end": v(6.23, -4.73) * mm});
            skLineSegment(sketch, "E758", {"start": v(6.23, -4.73) * mm, "end": v(6.27, -4.83) * mm});
            skLineSegment(sketch, "E759", {"start": v(6.27, -4.83) * mm, "end": v(5.77, -5.42) * mm});
            skLineSegment(sketch, "E760", {"start": v(5.77, -5.42) * mm, "end": v(5.67, -5.4) * mm});
            skLineSegment(sketch, "E761", {"start": v(5.67, -5.4) * mm, "end": v(5.53, -5.35) * mm});
            skLineSegment(sketch, "E762", {"start": v(5.53, -5.35) * mm, "end": v(5.4, -5.31) * mm});
            skLineSegment(sketch, "E763", {"start": v(5.4, -5.31) * mm, "end": v(5.28, -5.27) * mm});
            skLineSegment(sketch, "E764", {"start": v(5.28, -5.27) * mm, "end": v(5.16, -5.21) * mm});
            skLineSegment(sketch, "E765", {"start": v(5.16, -5.21) * mm, "end": v(5.04, -5.16) * mm});
            skLineSegment(sketch, "E766", {"start": v(5.04, -5.16) * mm, "end": v(4.93, -5.1) * mm});
            skLineSegment(sketch, "E767", {"start": v(4.93, -5.1) * mm, "end": v(4.83, -5.02) * mm});
            skLineSegment(sketch, "E768", {"start": v(4.83, -5.02) * mm, "end": v(4.78, -4.99) * mm});
            skLineSegment(sketch, "E769", {"start": v(4.78, -4.99) * mm, "end": v(4.72, -4.96) * mm});
            skLineSegment(sketch, "E770", {"start": v(4.72, -4.96) * mm, "end": v(4.65, -4.94) * mm});
            skLineSegment(sketch, "E771", {"start": v(4.65, -4.94) * mm, "end": v(4.61, -4.93) * mm});
            skLineSegment(sketch, "E772", {"start": v(4.61, -4.93) * mm, "end": v(4.57, -4.93) * mm});
            skLineSegment(sketch, "E773", {"start": v(4.57, -4.93) * mm, "end": v(4.49, -4.96) * mm});
            skLineSegment(sketch, "E774", {"start": v(4.49, -4.96) * mm, "end": v(4.04, -5.34) * mm});
            skLineSegment(sketch, "E775", {"start": v(4.04, -5.34) * mm, "end": v(3.99, -5.41) * mm});
            skLineSegment(sketch, "E776", {"start": v(3.99, -5.41) * mm, "end": v(3.98, -5.46) * mm});
            skLineSegment(sketch, "E777", {"start": v(3.98, -5.46) * mm, "end": v(3.98, -5.5) * mm});
            skLineSegment(sketch, "E778", {"start": v(3.98, -5.5) * mm, "end": v(3.99, -5.56) * mm});
            skLineSegment(sketch, "E779", {"start": v(3.99, -5.56) * mm, "end": v(4, -5.63) * mm});
            skLineSegment(sketch, "E780", {"start": v(4, -5.63) * mm, "end": v(4.03, -5.68) * mm});
            skLineSegment(sketch, "E781", {"start": v(4.03, -5.68) * mm, "end": v(4.08, -5.8) * mm});
            skLineSegment(sketch, "E782", {"start": v(4.08, -5.8) * mm, "end": v(4.12, -5.92) * mm});
            skLineSegment(sketch, "E783", {"start": v(4.12, -5.92) * mm, "end": v(4.15, -6.04) * mm});
            skLineSegment(sketch, "E784", {"start": v(4.15, -6.04) * mm, "end": v(4.18, -6.17) * mm});
            skLineSegment(sketch, "E785", {"start": v(4.18, -6.17) * mm, "end": v(4.2, -6.3) * mm});
            skLineSegment(sketch, "E786", {"start": v(4.2, -6.3) * mm, "end": v(4.22, -6.44) * mm});
            skLineSegment(sketch, "E787", {"start": v(4.22, -6.44) * mm, "end": v(4.24, -6.58) * mm});
            skLineSegment(sketch, "E788", {"start": v(4.24, -6.58) * mm, "end": v(4.24, -6.68) * mm});
            skLineSegment(sketch, "E789", {"start": v(4.24, -6.68) * mm, "end": v(3.57, -7.06) * mm});
            skLineSegment(sketch, "E790", {"start": v(3.57, -7.06) * mm, "end": v(3.48, -7) * mm});
            skLineSegment(sketch, "E791", {"start": v(3.48, -7) * mm, "end": v(3.37, -6.92) * mm});
            skLineSegment(sketch, "E792", {"start": v(3.37, -6.92) * mm, "end": v(3.26, -6.84) * mm});
            skLineSegment(sketch, "E793", {"start": v(3.26, -6.84) * mm, "end": v(3.16, -6.75) * mm});
            skLineSegment(sketch, "E794", {"start": v(3.16, -6.75) * mm, "end": v(3.06, -6.66) * mm});
            skLineSegment(sketch, "E795", {"start": v(3.06, -6.66) * mm, "end": v(2.97, -6.57) * mm});
            skLineSegment(sketch, "E796", {"start": v(2.97, -6.57) * mm, "end": v(2.9, -6.47) * mm});
            skLineSegment(sketch, "E797", {"start": v(2.9, -6.47) * mm, "end": v(2.82, -6.37) * mm});
            skLineSegment(sketch, "E798", {"start": v(2.82, -6.37) * mm, "end": v(2.78, -6.32) * mm});
            skLineSegment(sketch, "E799", {"start": v(2.78, -6.32) * mm, "end": v(2.73, -6.27) * mm});
            skLineSegment(sketch, "E800", {"start": v(2.73, -6.27) * mm, "end": v(2.68, -6.23) * mm});
            skLineSegment(sketch, "E801", {"start": v(2.68, -6.23) * mm, "end": v(2.65, -6.21) * mm});
            skLineSegment(sketch, "E802", {"start": v(2.65, -6.21) * mm, "end": v(2.6, -6.2) * mm});
            skLineSegment(sketch, "E803", {"start": v(2.6, -6.2) * mm, "end": v(2.52, -6.2) * mm});
            skLineSegment(sketch, "E804", {"start": v(2.52, -6.2) * mm, "end": v(1.97, -6.4) * mm});
            skLineSegment(sketch, "E805", {"start": v(1.97, -6.4) * mm, "end": v(1.9, -6.45) * mm});
            skLineSegment(sketch, "E806", {"start": v(1.9, -6.45) * mm, "end": v(1.87, -6.49) * mm});
            skLineSegment(sketch, "E807", {"start": v(1.87, -6.49) * mm, "end": v(1.86, -6.52) * mm});
            skLineSegment(sketch, "E808", {"start": v(1.86, -6.52) * mm, "end": v(1.85, -6.59) * mm});
            skLineSegment(sketch, "E809", {"start": v(1.85, -6.59) * mm, "end": v(1.84, -6.66) * mm});
            skLineSegment(sketch, "E810", {"start": v(1.84, -6.66) * mm, "end": v(1.84, -6.72) * mm});
            skLineSegment(sketch, "E811", {"start": v(1.84, -6.72) * mm, "end": v(1.85, -6.84) * mm});
            skLineSegment(sketch, "E812", {"start": v(1.85, -6.84) * mm, "end": v(1.85, -6.97) * mm});
            skLineSegment(sketch, "E813", {"start": v(1.85, -6.97) * mm, "end": v(1.84, -7.1) * mm});
            skLineSegment(sketch, "E814", {"start": v(1.84, -7.1) * mm, "end": v(1.82, -7.23) * mm});
            skLineSegment(sketch, "E815", {"start": v(1.82, -7.23) * mm, "end": v(1.8, -7.36) * mm});
            skLineSegment(sketch, "E816", {"start": v(1.8, -7.36) * mm, "end": v(1.77, -7.5) * mm});
            skLineSegment(sketch, "E817", {"start": v(1.77, -7.5) * mm, "end": v(1.73, -7.63) * mm});
            skLineSegment(sketch, "E818", {"start": v(1.73, -7.63) * mm, "end": v(1.7, -7.73) * mm});
            skLineSegment(sketch, "E819", {"start": v(1.7, -7.73) * mm, "end": v(0.94, -7.86) * mm});
            skLineSegment(sketch, "E820", {"start": v(0.94, -7.86) * mm, "end": v(0.87, -7.77) * mm});
            skLineSegment(sketch, "E821", {"start": v(0.87, -7.77) * mm, "end": v(0.8, -7.66) * mm});
            skLineSegment(sketch, "E822", {"start": v(0.8, -7.66) * mm, "end": v(0.72, -7.54) * mm});
            skLineSegment(sketch, "E823", {"start": v(0.72, -7.54) * mm, "end": v(0.66, -7.43) * mm});
            skLineSegment(sketch, "E824", {"start": v(0.66, -7.43) * mm, "end": v(0.6, -7.3) * mm});
            skLineSegment(sketch, "E825", {"start": v(0.6, -7.3) * mm, "end": v(0.55, -7.19) * mm});
            skLineSegment(sketch, "E826", {"start": v(0.55, -7.19) * mm, "end": v(0.5, -7.07) * mm});
            skLineSegment(sketch, "E827", {"start": v(0.5, -7.07) * mm, "end": v(0.47, -6.95) * mm});
            skLineSegment(sketch, "E828", {"start": v(0.47, -6.95) * mm, "end": v(0.45, -6.89) * mm});
            skLineSegment(sketch, "E829", {"start": v(0.45, -6.89) * mm, "end": v(0.42, -6.83) * mm});
            skLineSegment(sketch, "E830", {"start": v(0.42, -6.83) * mm, "end": v(0.39, -6.77) * mm});
            skLineSegment(sketch, "E831", {"start": v(0.39, -6.77) * mm, "end": v(0.36, -6.74) * mm});
            skLineSegment(sketch, "E832", {"start": v(0.36, -6.74) * mm, "end": v(0.33, -6.71) * mm});
            skLineSegment(sketch, "E833", {"start": v(0.33, -6.71) * mm, "end": v(0.25, -6.69) * mm});
            skLineSegment(sketch, "E834", {"start": v(0.25, -6.69) * mm, "end": v(-0.34, -6.68) * mm});
            skLineSegment(sketch, "E835", {"start": v(-0.34, -6.68) * mm, "end": v(-0.42, -6.7) * mm});
            skLineSegment(sketch, "E836", {"start": v(-0.42, -6.7) * mm, "end": v(-0.46, -6.74) * mm});
            skLineSegment(sketch, "E837", {"start": v(-0.46, -6.74) * mm, "end": v(-0.48, -6.77) * mm});
            skLineSegment(sketch, "E838", {"start": v(-0.48, -6.77) * mm, "end": v(-0.52, -6.82) * mm});
            skLineSegment(sketch, "E839", {"start": v(-0.52, -6.82) * mm, "end": v(-0.55, -6.88) * mm});
            skLineSegment(sketch, "E840", {"start": v(-0.55, -6.88) * mm, "end": v(-0.56, -6.94) * mm});
            skLineSegment(sketch, "E841", {"start": v(-0.56, -6.94) * mm, "end": v(-0.6, -7.06) * mm});
            skLineSegment(sketch, "E842", {"start": v(-0.6, -7.06) * mm, "end": v(-0.65, -7.18) * mm});
            skLineSegment(sketch, "E843", {"start": v(-0.65, -7.18) * mm, "end": v(-0.7, -7.3) * mm});
            skLineSegment(sketch, "E844", {"start": v(-0.7, -7.3) * mm, "end": v(-0.76, -7.42) * mm});
            skLineSegment(sketch, "E845", {"start": v(-0.76, -7.42) * mm, "end": v(-0.83, -7.53) * mm});
            skLineSegment(sketch, "E846", {"start": v(-0.83, -7.53) * mm, "end": v(-0.9, -7.65) * mm});
            skLineSegment(sketch, "E847", {"start": v(-0.9, -7.65) * mm, "end": v(-0.98, -7.76) * mm});
            skLineSegment(sketch, "E848", {"start": v(-0.98, -7.76) * mm, "end": v(-1.04, -7.84) * mm});
            skLineSegment(sketch, "E849", {"start": v(-1.04, -7.84) * mm, "end": v(-1.8, -7.7) * mm});
            skLineSegment(sketch, "E850", {"start": v(-1.8, -7.7) * mm, "end": v(-1.84, -7.6) * mm});
            skLineSegment(sketch, "E851", {"start": v(-1.84, -7.6) * mm, "end": v(-1.87, -7.47) * mm});
            skLineSegment(sketch, "E852", {"start": v(-1.87, -7.47) * mm, "end": v(-1.9, -7.34) * mm});
            skLineSegment(sketch, "E853", {"start": v(-1.9, -7.34) * mm, "end": v(-1.92, -7.2) * mm});
            skLineSegment(sketch, "E854", {"start": v(-1.92, -7.2) * mm, "end": v(-1.94, -7.07) * mm});
            skLineSegment(sketch, "E855", {"start": v(-1.94, -7.07) * mm, "end": v(-1.94, -6.94) * mm});
            skLineSegment(sketch, "E856", {"start": v(-1.94, -6.94) * mm, "end": v(-1.95, -6.82) * mm});
            skLineSegment(sketch, "E857", {"start": v(-1.95, -6.82) * mm, "end": v(-1.94, -6.7) * mm});
            skLineSegment(sketch, "E858", {"start": v(-1.94, -6.7) * mm, "end": v(-1.93, -6.63) * mm});
            skLineSegment(sketch, "E859", {"start": v(-1.93, -6.63) * mm, "end": v(-1.94, -6.56) * mm});
            skLineSegment(sketch, "E860", {"start": v(-1.94, -6.56) * mm, "end": v(-1.95, -6.5) * mm});
            skLineSegment(sketch, "E861", {"start": v(-1.95, -6.5) * mm, "end": v(-1.96, -6.46) * mm});
            skLineSegment(sketch, "E862", {"start": v(-1.96, -6.46) * mm, "end": v(-1.98, -6.42) * mm});
            skLineSegment(sketch, "E863", {"start": v(-1.98, -6.42) * mm, "end": v(-2.06, -6.37) * mm});
            skLineSegment(sketch, "E864", {"start": v(-2.06, -6.37) * mm, "end": v(-2.6, -6.16) * mm});
            skLineSegment(sketch, "E865", {"start": v(-2.6, -6.16) * mm, "end": v(-2.7, -6.16) * mm});
            skLineSegment(sketch, "E866", {"start": v(-2.7, -6.16) * mm, "end": v(-2.74, -6.17) * mm});
            skLineSegment(sketch, "E867", {"start": v(-2.74, -6.17) * mm, "end": v(-2.77, -6.2) * mm});
            skLineSegment(sketch, "E868", {"start": v(-2.77, -6.2) * mm, "end": v(-2.82, -6.23) * mm});
            skLineSegment(sketch, "E869", {"start": v(-2.82, -6.23) * mm, "end": v(-2.87, -6.28) * mm});
            skLineSegment(sketch, "E870", {"start": v(-2.87, -6.28) * mm, "end": v(-2.9, -6.33) * mm});
            skLineSegment(sketch, "E871", {"start": v(-2.9, -6.33) * mm, "end": v(-2.98, -6.43) * mm});
            skLineSegment(sketch, "E872", {"start": v(-2.98, -6.43) * mm, "end": v(-3.06, -6.53) * mm});
            skLineSegment(sketch, "E873", {"start": v(-3.06, -6.53) * mm, "end": v(-3.16, -6.62) * mm});
            skLineSegment(sketch, "E874", {"start": v(-3.16, -6.62) * mm, "end": v(-3.25, -6.7) * mm});
            skLineSegment(sketch, "E875", {"start": v(-3.25, -6.7) * mm, "end": v(-3.36, -6.8) * mm});
            skLineSegment(sketch, "E876", {"start": v(-3.36, -6.8) * mm, "end": v(-3.46, -6.88) * mm});
            skLineSegment(sketch, "E877", {"start": v(-3.46, -6.88) * mm, "end": v(-3.58, -6.96) * mm});
            skLineSegment(sketch, "E878", {"start": v(-3.58, -6.96) * mm, "end": v(-3.66, -7.01) * mm});
            skLineSegment(sketch, "E879", {"start": v(-3.66, -7.01) * mm, "end": v(-4.33, -6.62) * mm});
            skLineSegment(sketch, "E880", {"start": v(-4.33, -6.62) * mm, "end": v(-4.33, -6.52) * mm});
            skLineSegment(sketch, "E881", {"start": v(-4.33, -6.52) * mm, "end": v(-4.31, -6.38) * mm});
            skLineSegment(sketch, "E882", {"start": v(-4.31, -6.38) * mm, "end": v(-4.3, -6.24) * mm});
            skLineSegment(sketch, "E883", {"start": v(-4.3, -6.24) * mm, "end": v(-4.27, -6.11) * mm});
            skLineSegment(sketch, "E884", {"start": v(-4.27, -6.11) * mm, "end": v(-4.24, -5.98) * mm});
            skLineSegment(sketch, "E885", {"start": v(-4.24, -5.98) * mm, "end": v(-4.2, -5.86) * mm});
            skLineSegment(sketch, "E886", {"start": v(-4.2, -5.86) * mm, "end": v(-4.16, -5.74) * mm});
            skLineSegment(sketch, "E887", {"start": v(-4.16, -5.74) * mm, "end": v(-4.1, -5.62) * mm});
            skLineSegment(sketch, "E888", {"start": v(-4.1, -5.62) * mm, "end": v(-4.08, -5.57) * mm});
            skLineSegment(sketch, "E889", {"start": v(-4.08, -5.57) * mm, "end": v(-4.07, -5.5) * mm});
            skLineSegment(sketch, "E890", {"start": v(-4.07, -5.5) * mm, "end": v(-4.05, -5.44) * mm});
            skLineSegment(sketch, "E891", {"start": v(-4.05, -5.44) * mm, "end": v(-4.05, -5.4) * mm});
            skLineSegment(sketch, "E892", {"start": v(-4.05, -5.4) * mm, "end": v(-4.06, -5.36) * mm});
            skLineSegment(sketch, "E893", {"start": v(-4.06, -5.36) * mm, "end": v(-4.1, -5.28) * mm});
            skLineSegment(sketch, "E894", {"start": v(-4.1, -5.28) * mm, "end": v(-4.55, -4.9) * mm});
            skLineSegment(sketch, "E895", {"start": v(-4.55, -4.9) * mm, "end": v(-4.64, -4.87) * mm});
            skLineSegment(sketch, "E896", {"start": v(-4.64, -4.87) * mm, "end": v(-4.68, -4.87) * mm});
            skLineSegment(sketch, "E897", {"start": v(-4.68, -4.87) * mm, "end": v(-4.72, -4.87) * mm});
            skLineSegment(sketch, "E898", {"start": v(-4.72, -4.87) * mm, "end": v(-4.78, -4.9) * mm});
            skLineSegment(sketch, "E899", {"start": v(-4.78, -4.9) * mm, "end": v(-4.85, -4.92) * mm});
            skLineSegment(sketch, "E900", {"start": v(-4.85, -4.92) * mm, "end": v(-4.9, -4.96) * mm});
            skLineSegment(sketch, "E901", {"start": v(-4.9, -4.96) * mm, "end": v(-5, -5.02) * mm});
            skLineSegment(sketch, "E902", {"start": v(-5, -5.02) * mm, "end": v(-5.11, -5.09) * mm});
            skLineSegment(sketch, "E903", {"start": v(-5.11, -5.09) * mm, "end": v(-5.23, -5.14) * mm});
            skLineSegment(sketch, "E904", {"start": v(-5.23, -5.14) * mm, "end": v(-5.35, -5.2) * mm});
            skLineSegment(sketch, "E905", {"start": v(-5.35, -5.2) * mm, "end": v(-5.48, -5.24) * mm});
            skLineSegment(sketch, "E906", {"start": v(-5.48, -5.24) * mm, "end": v(-5.6, -5.28) * mm});
            skLineSegment(sketch, "E907", {"start": v(-5.6, -5.28) * mm, "end": v(-5.74, -5.31) * mm});
            skLineSegment(sketch, "E908", {"start": v(-5.74, -5.31) * mm, "end": v(-5.84, -5.34) * mm});
            skLineSegment(sketch, "E909", {"start": v(-5.84, -5.34) * mm, "end": v(-6.34, -4.74) * mm});
            skLineSegment(sketch, "E910", {"start": v(-6.34, -4.74) * mm, "end": v(-6.3, -4.64) * mm});
            skLineSegment(sketch, "E911", {"start": v(-6.3, -4.64) * mm, "end": v(-6.23, -4.52) * mm});
            skLineSegment(sketch, "E912", {"start": v(-6.23, -4.52) * mm, "end": v(-6.17, -4.4) * mm});
            skLineSegment(sketch, "E913", {"start": v(-6.17, -4.4) * mm, "end": v(-6.1, -4.28) * mm});
            skLineSegment(sketch, "E914", {"start": v(-6.1, -4.28) * mm, "end": v(-6.03, -4.17) * mm});
            skLineSegment(sketch, "E915", {"start": v(-6.03, -4.17) * mm, "end": v(-5.95, -4.07) * mm});
            skLineSegment(sketch, "E916", {"start": v(-5.95, -4.07) * mm, "end": v(-5.87, -3.97) * mm});
            skLineSegment(sketch, "E917", {"start": v(-5.87, -3.97) * mm, "end": v(-5.79, -3.88) * mm});
            skLineSegment(sketch, "E918", {"start": v(-5.79, -3.88) * mm, "end": v(-5.74, -3.84) * mm});
            skLineSegment(sketch, "E919", {"start": v(-5.74, -3.84) * mm, "end": v(-5.7, -3.78) * mm});
            skLineSegment(sketch, "E920", {"start": v(-5.7, -3.78) * mm, "end": v(-5.67, -3.72) * mm});
            skLineSegment(sketch, "E921", {"start": v(-5.67, -3.72) * mm, "end": v(-5.66, -3.69) * mm});
            skLineSegment(sketch, "E922", {"start": v(-5.66, -3.69) * mm, "end": v(-5.65, -3.64) * mm});
            skLineSegment(sketch, "E923", {"start": v(-5.65, -3.64) * mm, "end": v(-5.67, -3.56) * mm});
            skLineSegment(sketch, "E924", {"start": v(-5.67, -3.56) * mm, "end": v(-5.96, -3.05) * mm});
            skLineSegment(sketch, "E925", {"start": v(-5.96, -3.05) * mm, "end": v(-6.02, -2.99) * mm});
            skLineSegment(sketch, "E926", {"start": v(-6.02, -2.99) * mm, "end": v(-6.06, -2.97) * mm});
            skLineSegment(sketch, "E927", {"start": v(-6.06, -2.97) * mm, "end": v(-6.1, -2.96) * mm});
            skLineSegment(sketch, "E928", {"start": v(-6.1, -2.96) * mm, "end": v(-6.17, -2.96) * mm});
            skLineSegment(sketch, "E929", {"start": v(-6.17, -2.96) * mm, "end": v(-6.24, -2.96) * mm});
            skLineSegment(sketch, "E930", {"start": v(-6.24, -2.96) * mm, "end": v(-6.3, -2.98) * mm});
            skLineSegment(sketch, "E931", {"start": v(-6.3, -2.98) * mm, "end": v(-6.42, -3.01) * mm});
            skLineSegment(sketch, "E932", {"start": v(-6.42, -3.01) * mm, "end": v(-6.54, -3.03) * mm});
            skLineSegment(sketch, "E933", {"start": v(-6.54, -3.03) * mm, "end": v(-6.67, -3.04) * mm});
            skLineSegment(sketch, "E934", {"start": v(-6.67, -3.04) * mm, "end": v(-6.8, -3.05) * mm});
            skLineSegment(sketch, "E935", {"start": v(-6.8, -3.05) * mm, "end": v(-6.94, -3.05) * mm});
            skLineSegment(sketch, "E936", {"start": v(-6.94, -3.05) * mm, "end": v(-7.07, -3.04) * mm});
            skLineSegment(sketch, "E937", {"start": v(-7.07, -3.04) * mm, "end": v(-7.21, -3.03) * mm});
            skLineSegment(sketch, "E938", {"start": v(-7.21, -3.03) * mm, "end": v(-7.32, -3.02) * mm});
            skLineSegment(sketch, "E939", {"start": v(-7.32, -3.02) * mm, "end": v(-7.58, -2.29) * mm});
            skLineSegment(sketch, "E940", {"start": v(-7.58, -2.29) * mm, "end": v(-7.5, -2.2) * mm});
            skLineSegment(sketch, "E941", {"start": v(-7.5, -2.2) * mm, "end": v(-7.4, -2.11) * mm});
            skLineSegment(sketch, "E942", {"start": v(-7.4, -2.11) * mm, "end": v(-7.3, -2.02) * mm});
            skLineSegment(sketch, "E943", {"start": v(-7.3, -2.02) * mm, "end": v(-7.2, -1.94) * mm});
            skLineSegment(sketch, "E944", {"start": v(-7.2, -1.94) * mm, "end": v(-7.1, -1.86) * mm});
            skLineSegment(sketch, "E945", {"start": v(-7.1, -1.86) * mm, "end": v(-6.99, -1.79) * mm});
            skLineSegment(sketch, "E946", {"start": v(-6.99, -1.79) * mm, "end": v(-6.88, -1.72) * mm});
            skLineSegment(sketch, "E947", {"start": v(-6.88, -1.72) * mm, "end": v(-6.76, -1.67) * mm});
            skLineSegment(sketch, "E948", {"start": v(-6.76, -1.67) * mm, "end": v(-6.7, -1.64) * mm});
            skLineSegment(sketch, "E949", {"start": v(-6.7, -1.64) * mm, "end": v(-6.65, -1.6) * mm});
            skLineSegment(sketch, "E950", {"start": v(-6.65, -1.6) * mm, "end": v(-6.6, -1.56) * mm});
            skLineSegment(sketch, "E951", {"start": v(-6.6, -1.56) * mm, "end": v(-6.58, -1.53) * mm});
            skLineSegment(sketch, "E952", {"start": v(-6.58, -1.53) * mm, "end": v(-6.55, -1.5) * mm});
            skLineSegment(sketch, "E953", {"start": v(-6.55, -1.5) * mm, "end": v(-6.54, -1.4) * mm});
            skLineSegment(sketch, "E954", {"start": v(-6.54, -1.4) * mm, "end": v(-6.64, -0.83) * mm});
            skCircle(sketch, "E955", {"center": v(0, 0) * mm, "radius": 1 * mm});
            skSolve(sketch);
        }
        {
            var Q0;
            Q0 = qSketchRegion(id + "F2", true);
            var Q1;
            Q1=makeQuery(id+"F2.imprint","IMPRINT",FACE,{"disambiguationData":[TD([[makeQuery(id+"F2.imprint","IMPRINT",EDGE,{"derivedFrom":sQuery(id+"F2.wireOp",EDGE,"E415")}),-1.0]])]});
            extrude(context, id + "F3", {"entities" : qUnion([Q0, Q1]), "depth" : 4 * mm});
        }
        {
            var Q0;
            Q0=makeQuery(id+"F3.opExtrude","SWEPT_BODY",BODY,{"disambiguationData":[OSD([sQuery(id+"F2.wireOp",EDGE,"E415"),sQuery(id+"F2.wireOp",EDGE,"E416"),sQuery(id+"F2.wireOp",EDGE,"E417"),sQuery(id+"F2.wireOp",EDGE,"E418"),sQuery(id+"F2.wireOp",EDGE,"E419"),sQuery(id+"F2.wireOp",EDGE,"E420"),sQuery(id+"F2.wireOp",EDGE,"E421"),sQuery(id+"F2.wireOp",EDGE,"E422"),sQuery(id+"F2.wireOp",EDGE,"E423"),sQuery(id+"F2.wireOp",EDGE,"E424"),sQuery(id+"F2.wireOp",EDGE,"E425"),sQuery(id+"F2.wireOp",EDGE,"E426"),sQuery(id+"F2.wireOp",EDGE,"E427"),sQuery(id+"F2.wireOp",EDGE,"E428"),sQuery(id+"F2.wireOp",EDGE,"E429"),sQuery(id+"F2.wireOp",EDGE,"E430"),sQuery(id+"F2.wireOp",EDGE,"E431"),sQuery(id+"F2.wireOp",EDGE,"E432"),sQuery(id+"F2.wireOp",EDGE,"E433"),sQuery(id+"F2.wireOp",EDGE,"E434"),sQuery(id+"F2.wireOp",EDGE,"E435"),sQuery(id+"F2.wireOp",EDGE,"E436"),sQuery(id+"F2.wireOp",EDGE,"E437"),sQuery(id+"F2.wireOp",EDGE,"E438"),sQuery(id+"F2.wireOp",EDGE,"E439"),sQuery(id+"F2.wireOp",EDGE,"E440"),sQuery(id+"F2.wireOp",EDGE,"E441"),sQuery(id+"F2.wireOp",EDGE,"E442"),sQuery(id+"F2.wireOp",EDGE,"E443"),sQuery(id+"F2.wireOp",EDGE,"E444"),sQuery(id+"F2.wireOp",EDGE,"E445"),sQuery(id+"F2.wireOp",EDGE,"E446"),sQuery(id+"F2.wireOp",EDGE,"E447"),sQuery(id+"F2.wireOp",EDGE,"E448"),sQuery(id+"F2.wireOp",EDGE,"E449"),sQuery(id+"F2.wireOp",EDGE,"E450"),sQuery(id+"F2.wireOp",EDGE,"E451"),sQuery(id+"F2.wireOp",EDGE,"E452"),sQuery(id+"F2.wireOp",EDGE,"E453"),sQuery(id+"F2.wireOp",EDGE,"E454"),sQuery(id+"F2.wireOp",EDGE,"E455"),sQuery(id+"F2.wireOp",EDGE,"E456"),sQuery(id+"F2.wireOp",EDGE,"E457"),sQuery(id+"F2.wireOp",EDGE,"E458"),sQuery(id+"F2.wireOp",EDGE,"E459"),sQuery(id+"F2.wireOp",EDGE,"E460"),sQuery(id+"F2.wireOp",EDGE,"E461"),sQuery(id+"F2.wireOp",EDGE,"E462"),sQuery(id+"F2.wireOp",EDGE,"E463"),sQuery(id+"F2.wireOp",EDGE,"E464"),sQuery(id+"F2.wireOp",EDGE,"E465"),sQuery(id+"F2.wireOp",EDGE,"E466"),sQuery(id+"F2.wireOp",EDGE,"E467"),sQuery(id+"F2.wireOp",EDGE,"E468"),sQuery(id+"F2.wireOp",EDGE,"E469"),sQuery(id+"F2.wireOp",EDGE,"E470"),sQuery(id+"F2.wireOp",EDGE,"E471"),sQuery(id+"F2.wireOp",EDGE,"E472"),sQuery(id+"F2.wireOp",EDGE,"E473"),sQuery(id+"F2.wireOp",EDGE,"E474"),sQuery(id+"F2.wireOp",EDGE,"E475"),sQuery(id+"F2.wireOp",EDGE,"E476"),sQuery(id+"F2.wireOp",EDGE,"E477"),sQuery(id+"F2.wireOp",EDGE,"E478"),sQuery(id+"F2.wireOp",EDGE,"E479"),sQuery(id+"F2.wireOp",EDGE,"E480"),sQuery(id+"F2.wireOp",EDGE,"E481"),sQuery(id+"F2.wireOp",EDGE,"E482"),sQuery(id+"F2.wireOp",EDGE,"E483"),sQuery(id+"F2.wireOp",EDGE,"E484"),sQuery(id+"F2.wireOp",EDGE,"E485"),sQuery(id+"F2.wireOp",EDGE,"E486"),sQuery(id+"F2.wireOp",EDGE,"E487"),sQuery(id+"F2.wireOp",EDGE,"E488"),sQuery(id+"F2.wireOp",EDGE,"E489"),sQuery(id+"F2.wireOp",EDGE,"E490"),sQuery(id+"F2.wireOp",EDGE,"E491"),sQuery(id+"F2.wireOp",EDGE,"E492"),sQuery(id+"F2.wireOp",EDGE,"E493"),sQuery(id+"F2.wireOp",EDGE,"E494"),sQuery(id+"F2.wireOp",EDGE,"E495"),sQuery(id+"F2.wireOp",EDGE,"E496"),sQuery(id+"F2.wireOp",EDGE,"E497"),sQuery(id+"F2.wireOp",EDGE,"E498"),sQuery(id+"F2.wireOp",EDGE,"E499"),sQuery(id+"F2.wireOp",EDGE,"E500"),sQuery(id+"F2.wireOp",EDGE,"E501"),sQuery(id+"F2.wireOp",EDGE,"E502"),sQuery(id+"F2.wireOp",EDGE,"E503"),sQuery(id+"F2.wireOp",EDGE,"E504"),sQuery(id+"F2.wireOp",EDGE,"E505"),sQuery(id+"F2.wireOp",EDGE,"E506"),sQuery(id+"F2.wireOp",EDGE,"E507"),sQuery(id+"F2.wireOp",EDGE,"E508"),sQuery(id+"F2.wireOp",EDGE,"E509"),sQuery(id+"F2.wireOp",EDGE,"E510"),sQuery(id+"F2.wireOp",EDGE,"E511"),sQuery(id+"F2.wireOp",EDGE,"E512"),sQuery(id+"F2.wireOp",EDGE,"E513"),sQuery(id+"F2.wireOp",EDGE,"E514"),sQuery(id+"F2.wireOp",EDGE,"E515"),sQuery(id+"F2.wireOp",EDGE,"E516"),sQuery(id+"F2.wireOp",EDGE,"E517"),sQuery(id+"F2.wireOp",EDGE,"E518"),sQuery(id+"F2.wireOp",EDGE,"E519"),sQuery(id+"F2.wireOp",EDGE,"E520"),sQuery(id+"F2.wireOp",EDGE,"E521"),sQuery(id+"F2.wireOp",EDGE,"E522"),sQuery(id+"F2.wireOp",EDGE,"E523"),sQuery(id+"F2.wireOp",EDGE,"E524"),sQuery(id+"F2.wireOp",EDGE,"E525"),sQuery(id+"F2.wireOp",EDGE,"E526"),sQuery(id+"F2.wireOp",EDGE,"E527"),sQuery(id+"F2.wireOp",EDGE,"E528"),sQuery(id+"F2.wireOp",EDGE,"E529"),sQuery(id+"F2.wireOp",EDGE,"E530"),sQuery(id+"F2.wireOp",EDGE,"E531"),sQuery(id+"F2.wireOp",EDGE,"E532"),sQuery(id+"F2.wireOp",EDGE,"E533"),sQuery(id+"F2.wireOp",EDGE,"E534"),sQuery(id+"F2.wireOp",EDGE,"E535"),sQuery(id+"F2.wireOp",EDGE,"E536"),sQuery(id+"F2.wireOp",EDGE,"E537"),sQuery(id+"F2.wireOp",EDGE,"E538"),sQuery(id+"F2.wireOp",EDGE,"E539"),sQuery(id+"F2.wireOp",EDGE,"E540"),sQuery(id+"F2.wireOp",EDGE,"E541"),sQuery(id+"F2.wireOp",EDGE,"E542"),sQuery(id+"F2.wireOp",EDGE,"E543"),sQuery(id+"F2.wireOp",EDGE,"E544"),sQuery(id+"F2.wireOp",EDGE,"E545"),sQuery(id+"F2.wireOp",EDGE,"E546"),sQuery(id+"F2.wireOp",EDGE,"E547"),sQuery(id+"F2.wireOp",EDGE,"E548"),sQuery(id+"F2.wireOp",EDGE,"E549"),sQuery(id+"F2.wireOp",EDGE,"E550"),sQuery(id+"F2.wireOp",EDGE,"E551"),sQuery(id+"F2.wireOp",EDGE,"E552"),sQuery(id+"F2.wireOp",EDGE,"E553"),sQuery(id+"F2.wireOp",EDGE,"E554"),sQuery(id+"F2.wireOp",EDGE,"E555"),sQuery(id+"F2.wireOp",EDGE,"E556"),sQuery(id+"F2.wireOp",EDGE,"E557"),sQuery(id+"F2.wireOp",EDGE,"E558"),sQuery(id+"F2.wireOp",EDGE,"E559"),sQuery(id+"F2.wireOp",EDGE,"E560"),sQuery(id+"F2.wireOp",EDGE,"E561"),sQuery(id+"F2.wireOp",EDGE,"E562"),sQuery(id+"F2.wireOp",EDGE,"E563"),sQuery(id+"F2.wireOp",EDGE,"E564"),sQuery(id+"F2.wireOp",EDGE,"E565"),sQuery(id+"F2.wireOp",EDGE,"E566"),sQuery(id+"F2.wireOp",EDGE,"E567"),sQuery(id+"F2.wireOp",EDGE,"E568"),sQuery(id+"F2.wireOp",EDGE,"E569"),sQuery(id+"F2.wireOp",EDGE,"E570"),sQuery(id+"F2.wireOp",EDGE,"E571"),sQuery(id+"F2.wireOp",EDGE,"E572"),sQuery(id+"F2.wireOp",EDGE,"E573"),sQuery(id+"F2.wireOp",EDGE,"E574"),sQuery(id+"F2.wireOp",EDGE,"E575"),sQuery(id+"F2.wireOp",EDGE,"E576"),sQuery(id+"F2.wireOp",EDGE,"E577"),sQuery(id+"F2.wireOp",EDGE,"E578"),sQuery(id+"F2.wireOp",EDGE,"E579"),sQuery(id+"F2.wireOp",EDGE,"E580"),sQuery(id+"F2.wireOp",EDGE,"E581"),sQuery(id+"F2.wireOp",EDGE,"E582"),sQuery(id+"F2.wireOp",EDGE,"E583"),sQuery(id+"F2.wireOp",EDGE,"E584"),sQuery(id+"F2.wireOp",EDGE,"E585"),sQuery(id+"F2.wireOp",EDGE,"E586"),sQuery(id+"F2.wireOp",EDGE,"E587"),sQuery(id+"F2.wireOp",EDGE,"E588"),sQuery(id+"F2.wireOp",EDGE,"E589"),sQuery(id+"F2.wireOp",EDGE,"E590"),sQuery(id+"F2.wireOp",EDGE,"E591"),sQuery(id+"F2.wireOp",EDGE,"E592"),sQuery(id+"F2.wireOp",EDGE,"E593"),sQuery(id+"F2.wireOp",EDGE,"E594"),sQuery(id+"F2.wireOp",EDGE,"E595"),sQuery(id+"F2.wireOp",EDGE,"E596"),sQuery(id+"F2.wireOp",EDGE,"E597"),sQuery(id+"F2.wireOp",EDGE,"E598"),sQuery(id+"F2.wireOp",EDGE,"E599"),sQuery(id+"F2.wireOp",EDGE,"E600"),sQuery(id+"F2.wireOp",EDGE,"E601"),sQuery(id+"F2.wireOp",EDGE,"E602"),sQuery(id+"F2.wireOp",EDGE,"E603"),sQuery(id+"F2.wireOp",EDGE,"E604"),sQuery(id+"F2.wireOp",EDGE,"E605"),sQuery(id+"F2.wireOp",EDGE,"E606"),sQuery(id+"F2.wireOp",EDGE,"E607"),sQuery(id+"F2.wireOp",EDGE,"E608"),sQuery(id+"F2.wireOp",EDGE,"E609"),sQuery(id+"F2.wireOp",EDGE,"E610"),sQuery(id+"F2.wireOp",EDGE,"E611"),sQuery(id+"F2.wireOp",EDGE,"E612"),sQuery(id+"F2.wireOp",EDGE,"E613"),sQuery(id+"F2.wireOp",EDGE,"E614"),sQuery(id+"F2.wireOp",EDGE,"E615"),sQuery(id+"F2.wireOp",EDGE,"E616"),sQuery(id+"F2.wireOp",EDGE,"E617"),sQuery(id+"F2.wireOp",EDGE,"E618"),sQuery(id+"F2.wireOp",EDGE,"E619"),sQuery(id+"F2.wireOp",EDGE,"E620"),sQuery(id+"F2.wireOp",EDGE,"E621"),sQuery(id+"F2.wireOp",EDGE,"E622"),sQuery(id+"F2.wireOp",EDGE,"E623"),sQuery(id+"F2.wireOp",EDGE,"E624"),sQuery(id+"F2.wireOp",EDGE,"E625"),sQuery(id+"F2.wireOp",EDGE,"E626"),sQuery(id+"F2.wireOp",EDGE,"E627"),sQuery(id+"F2.wireOp",EDGE,"E628"),sQuery(id+"F2.wireOp",EDGE,"E629"),sQuery(id+"F2.wireOp",EDGE,"E630"),sQuery(id+"F2.wireOp",EDGE,"E631"),sQuery(id+"F2.wireOp",EDGE,"E632"),sQuery(id+"F2.wireOp",EDGE,"E633"),sQuery(id+"F2.wireOp",EDGE,"E634"),sQuery(id+"F2.wireOp",EDGE,"E635"),sQuery(id+"F2.wireOp",EDGE,"E636"),sQuery(id+"F2.wireOp",EDGE,"E637"),sQuery(id+"F2.wireOp",EDGE,"E638"),sQuery(id+"F2.wireOp",EDGE,"E639"),sQuery(id+"F2.wireOp",EDGE,"E640"),sQuery(id+"F2.wireOp",EDGE,"E641"),sQuery(id+"F2.wireOp",EDGE,"E642"),sQuery(id+"F2.wireOp",EDGE,"E643"),sQuery(id+"F2.wireOp",EDGE,"E644"),sQuery(id+"F2.wireOp",EDGE,"E645"),sQuery(id+"F2.wireOp",EDGE,"E646"),sQuery(id+"F2.wireOp",EDGE,"E647"),sQuery(id+"F2.wireOp",EDGE,"E648"),sQuery(id+"F2.wireOp",EDGE,"E649"),sQuery(id+"F2.wireOp",EDGE,"E650"),sQuery(id+"F2.wireOp",EDGE,"E651"),sQuery(id+"F2.wireOp",EDGE,"E652"),sQuery(id+"F2.wireOp",EDGE,"E653"),sQuery(id+"F2.wireOp",EDGE,"E654"),sQuery(id+"F2.wireOp",EDGE,"E655"),sQuery(id+"F2.wireOp",EDGE,"E656"),sQuery(id+"F2.wireOp",EDGE,"E657"),sQuery(id+"F2.wireOp",EDGE,"E658"),sQuery(id+"F2.wireOp",EDGE,"E659"),sQuery(id+"F2.wireOp",EDGE,"E660"),sQuery(id+"F2.wireOp",EDGE,"E661"),sQuery(id+"F2.wireOp",EDGE,"E662"),sQuery(id+"F2.wireOp",EDGE,"E663"),sQuery(id+"F2.wireOp",EDGE,"E664"),sQuery(id+"F2.wireOp",EDGE,"E665"),sQuery(id+"F2.wireOp",EDGE,"E666"),sQuery(id+"F2.wireOp",EDGE,"E667"),sQuery(id+"F2.wireOp",EDGE,"E668"),sQuery(id+"F2.wireOp",EDGE,"E669"),sQuery(id+"F2.wireOp",EDGE,"E670"),sQuery(id+"F2.wireOp",EDGE,"E671"),sQuery(id+"F2.wireOp",EDGE,"E672"),sQuery(id+"F2.wireOp",EDGE,"E673"),sQuery(id+"F2.wireOp",EDGE,"E674"),sQuery(id+"F2.wireOp",EDGE,"E675"),sQuery(id+"F2.wireOp",EDGE,"E676"),sQuery(id+"F2.wireOp",EDGE,"E677"),sQuery(id+"F2.wireOp",EDGE,"E678"),sQuery(id+"F2.wireOp",EDGE,"E679"),sQuery(id+"F2.wireOp",EDGE,"E680"),sQuery(id+"F2.wireOp",EDGE,"E681"),sQuery(id+"F2.wireOp",EDGE,"E682"),sQuery(id+"F2.wireOp",EDGE,"E683"),sQuery(id+"F2.wireOp",EDGE,"E684"),sQuery(id+"F2.wireOp",EDGE,"E685"),sQuery(id+"F2.wireOp",EDGE,"E686"),sQuery(id+"F2.wireOp",EDGE,"E687"),sQuery(id+"F2.wireOp",EDGE,"E688"),sQuery(id+"F2.wireOp",EDGE,"E689"),sQuery(id+"F2.wireOp",EDGE,"E690"),sQuery(id+"F2.wireOp",EDGE,"E691"),sQuery(id+"F2.wireOp",EDGE,"E692"),sQuery(id+"F2.wireOp",EDGE,"E693"),sQuery(id+"F2.wireOp",EDGE,"E694"),sQuery(id+"F2.wireOp",EDGE,"E695"),sQuery(id+"F2.wireOp",EDGE,"E696"),sQuery(id+"F2.wireOp",EDGE,"E697"),sQuery(id+"F2.wireOp",EDGE,"E698"),sQuery(id+"F2.wireOp",EDGE,"E699"),sQuery(id+"F2.wireOp",EDGE,"E700"),sQuery(id+"F2.wireOp",EDGE,"E701"),sQuery(id+"F2.wireOp",EDGE,"E702"),sQuery(id+"F2.wireOp",EDGE,"E703"),sQuery(id+"F2.wireOp",EDGE,"E704"),sQuery(id+"F2.wireOp",EDGE,"E705"),sQuery(id+"F2.wireOp",EDGE,"E706"),sQuery(id+"F2.wireOp",EDGE,"E707"),sQuery(id+"F2.wireOp",EDGE,"E708"),sQuery(id+"F2.wireOp",EDGE,"E709"),sQuery(id+"F2.wireOp",EDGE,"E710"),sQuery(id+"F2.wireOp",EDGE,"E711"),sQuery(id+"F2.wireOp",EDGE,"E712"),sQuery(id+"F2.wireOp",EDGE,"E713"),sQuery(id+"F2.wireOp",EDGE,"E714"),sQuery(id+"F2.wireOp",EDGE,"E715"),sQuery(id+"F2.wireOp",EDGE,"E716"),sQuery(id+"F2.wireOp",EDGE,"E717"),sQuery(id+"F2.wireOp",EDGE,"E718"),sQuery(id+"F2.wireOp",EDGE,"E719"),sQuery(id+"F2.wireOp",EDGE,"E720"),sQuery(id+"F2.wireOp",EDGE,"E721"),sQuery(id+"F2.wireOp",EDGE,"E722"),sQuery(id+"F2.wireOp",EDGE,"E723"),sQuery(id+"F2.wireOp",EDGE,"E724"),sQuery(id+"F2.wireOp",EDGE,"E725"),sQuery(id+"F2.wireOp",EDGE,"E726"),sQuery(id+"F2.wireOp",EDGE,"E727"),sQuery(id+"F2.wireOp",EDGE,"E728"),sQuery(id+"F2.wireOp",EDGE,"E729"),sQuery(id+"F2.wireOp",EDGE,"E730"),sQuery(id+"F2.wireOp",EDGE,"E731"),sQuery(id+"F2.wireOp",EDGE,"E732"),sQuery(id+"F2.wireOp",EDGE,"E733"),sQuery(id+"F2.wireOp",EDGE,"E734"),sQuery(id+"F2.wireOp",EDGE,"E735"),sQuery(id+"F2.wireOp",EDGE,"E736"),sQuery(id+"F2.wireOp",EDGE,"E737"),sQuery(id+"F2.wireOp",EDGE,"E738"),sQuery(id+"F2.wireOp",EDGE,"E739"),sQuery(id+"F2.wireOp",EDGE,"E740"),sQuery(id+"F2.wireOp",EDGE,"E741"),sQuery(id+"F2.wireOp",EDGE,"E742"),sQuery(id+"F2.wireOp",EDGE,"E743"),sQuery(id+"F2.wireOp",EDGE,"E744"),sQuery(id+"F2.wireOp",EDGE,"E745"),sQuery(id+"F2.wireOp",EDGE,"E746"),sQuery(id+"F2.wireOp",EDGE,"E747"),sQuery(id+"F2.wireOp",EDGE,"E748"),sQuery(id+"F2.wireOp",EDGE,"E749"),sQuery(id+"F2.wireOp",EDGE,"E750"),sQuery(id+"F2.wireOp",EDGE,"E751"),sQuery(id+"F2.wireOp",EDGE,"E752"),sQuery(id+"F2.wireOp",EDGE,"E753"),sQuery(id+"F2.wireOp",EDGE,"E754"),sQuery(id+"F2.wireOp",EDGE,"E755"),sQuery(id+"F2.wireOp",EDGE,"E756"),sQuery(id+"F2.wireOp",EDGE,"E757"),sQuery(id+"F2.wireOp",EDGE,"E758"),sQuery(id+"F2.wireOp",EDGE,"E759"),sQuery(id+"F2.wireOp",EDGE,"E760"),sQuery(id+"F2.wireOp",EDGE,"E761"),sQuery(id+"F2.wireOp",EDGE,"E762"),sQuery(id+"F2.wireOp",EDGE,"E763"),sQuery(id+"F2.wireOp",EDGE,"E764"),sQuery(id+"F2.wireOp",EDGE,"E765"),sQuery(id+"F2.wireOp",EDGE,"E766"),sQuery(id+"F2.wireOp",EDGE,"E767"),sQuery(id+"F2.wireOp",EDGE,"E768"),sQuery(id+"F2.wireOp",EDGE,"E769"),sQuery(id+"F2.wireOp",EDGE,"E770"),sQuery(id+"F2.wireOp",EDGE,"E771"),sQuery(id+"F2.wireOp",EDGE,"E772"),sQuery(id+"F2.wireOp",EDGE,"E773"),sQuery(id+"F2.wireOp",EDGE,"E774"),sQuery(id+"F2.wireOp",EDGE,"E775"),sQuery(id+"F2.wireOp",EDGE,"E776"),sQuery(id+"F2.wireOp",EDGE,"E777"),sQuery(id+"F2.wireOp",EDGE,"E778"),sQuery(id+"F2.wireOp",EDGE,"E779"),sQuery(id+"F2.wireOp",EDGE,"E780"),sQuery(id+"F2.wireOp",EDGE,"E781"),sQuery(id+"F2.wireOp",EDGE,"E782"),sQuery(id+"F2.wireOp",EDGE,"E783"),sQuery(id+"F2.wireOp",EDGE,"E784"),sQuery(id+"F2.wireOp",EDGE,"E785"),sQuery(id+"F2.wireOp",EDGE,"E786"),sQuery(id+"F2.wireOp",EDGE,"E787"),sQuery(id+"F2.wireOp",EDGE,"E788"),sQuery(id+"F2.wireOp",EDGE,"E789"),sQuery(id+"F2.wireOp",EDGE,"E790"),sQuery(id+"F2.wireOp",EDGE,"E791"),sQuery(id+"F2.wireOp",EDGE,"E792"),sQuery(id+"F2.wireOp",EDGE,"E793"),sQuery(id+"F2.wireOp",EDGE,"E794"),sQuery(id+"F2.wireOp",EDGE,"E795"),sQuery(id+"F2.wireOp",EDGE,"E796"),sQuery(id+"F2.wireOp",EDGE,"E797"),sQuery(id+"F2.wireOp",EDGE,"E798"),sQuery(id+"F2.wireOp",EDGE,"E799"),sQuery(id+"F2.wireOp",EDGE,"E800"),sQuery(id+"F2.wireOp",EDGE,"E801"),sQuery(id+"F2.wireOp",EDGE,"E802"),sQuery(id+"F2.wireOp",EDGE,"E803"),sQuery(id+"F2.wireOp",EDGE,"E804"),sQuery(id+"F2.wireOp",EDGE,"E805"),sQuery(id+"F2.wireOp",EDGE,"E806"),sQuery(id+"F2.wireOp",EDGE,"E807"),sQuery(id+"F2.wireOp",EDGE,"E808"),sQuery(id+"F2.wireOp",EDGE,"E809"),sQuery(id+"F2.wireOp",EDGE,"E810"),sQuery(id+"F2.wireOp",EDGE,"E811"),sQuery(id+"F2.wireOp",EDGE,"E812"),sQuery(id+"F2.wireOp",EDGE,"E813"),sQuery(id+"F2.wireOp",EDGE,"E814"),sQuery(id+"F2.wireOp",EDGE,"E815"),sQuery(id+"F2.wireOp",EDGE,"E816"),sQuery(id+"F2.wireOp",EDGE,"E817"),sQuery(id+"F2.wireOp",EDGE,"E818"),sQuery(id+"F2.wireOp",EDGE,"E819"),sQuery(id+"F2.wireOp",EDGE,"E820"),sQuery(id+"F2.wireOp",EDGE,"E821"),sQuery(id+"F2.wireOp",EDGE,"E822"),sQuery(id+"F2.wireOp",EDGE,"E823"),sQuery(id+"F2.wireOp",EDGE,"E824"),sQuery(id+"F2.wireOp",EDGE,"E825"),sQuery(id+"F2.wireOp",EDGE,"E826"),sQuery(id+"F2.wireOp",EDGE,"E827"),sQuery(id+"F2.wireOp",EDGE,"E828"),sQuery(id+"F2.wireOp",EDGE,"E829"),sQuery(id+"F2.wireOp",EDGE,"E830"),sQuery(id+"F2.wireOp",EDGE,"E831"),sQuery(id+"F2.wireOp",EDGE,"E832"),sQuery(id+"F2.wireOp",EDGE,"E833"),sQuery(id+"F2.wireOp",EDGE,"E834"),sQuery(id+"F2.wireOp",EDGE,"E835"),sQuery(id+"F2.wireOp",EDGE,"E836"),sQuery(id+"F2.wireOp",EDGE,"E837"),sQuery(id+"F2.wireOp",EDGE,"E838"),sQuery(id+"F2.wireOp",EDGE,"E839"),sQuery(id+"F2.wireOp",EDGE,"E840"),sQuery(id+"F2.wireOp",EDGE,"E841"),sQuery(id+"F2.wireOp",EDGE,"E842"),sQuery(id+"F2.wireOp",EDGE,"E843"),sQuery(id+"F2.wireOp",EDGE,"E844"),sQuery(id+"F2.wireOp",EDGE,"E845"),sQuery(id+"F2.wireOp",EDGE,"E846"),sQuery(id+"F2.wireOp",EDGE,"E847"),sQuery(id+"F2.wireOp",EDGE,"E848"),sQuery(id+"F2.wireOp",EDGE,"E849"),sQuery(id+"F2.wireOp",EDGE,"E850"),sQuery(id+"F2.wireOp",EDGE,"E851"),sQuery(id+"F2.wireOp",EDGE,"E852"),sQuery(id+"F2.wireOp",EDGE,"E853"),sQuery(id+"F2.wireOp",EDGE,"E854"),sQuery(id+"F2.wireOp",EDGE,"E855"),sQuery(id+"F2.wireOp",EDGE,"E856"),sQuery(id+"F2.wireOp",EDGE,"E857"),sQuery(id+"F2.wireOp",EDGE,"E858"),sQuery(id+"F2.wireOp",EDGE,"E859"),sQuery(id+"F2.wireOp",EDGE,"E860"),sQuery(id+"F2.wireOp",EDGE,"E861"),sQuery(id+"F2.wireOp",EDGE,"E862"),sQuery(id+"F2.wireOp",EDGE,"E863"),sQuery(id+"F2.wireOp",EDGE,"E864"),sQuery(id+"F2.wireOp",EDGE,"E865"),sQuery(id+"F2.wireOp",EDGE,"E866"),sQuery(id+"F2.wireOp",EDGE,"E867"),sQuery(id+"F2.wireOp",EDGE,"E868"),sQuery(id+"F2.wireOp",EDGE,"E869"),sQuery(id+"F2.wireOp",EDGE,"E870"),sQuery(id+"F2.wireOp",EDGE,"E871"),sQuery(id+"F2.wireOp",EDGE,"E872"),sQuery(id+"F2.wireOp",EDGE,"E873"),sQuery(id+"F2.wireOp",EDGE,"E874"),sQuery(id+"F2.wireOp",EDGE,"E875"),sQuery(id+"F2.wireOp",EDGE,"E876"),sQuery(id+"F2.wireOp",EDGE,"E877"),sQuery(id+"F2.wireOp",EDGE,"E878"),sQuery(id+"F2.wireOp",EDGE,"E879"),sQuery(id+"F2.wireOp",EDGE,"E880"),sQuery(id+"F2.wireOp",EDGE,"E881"),sQuery(id+"F2.wireOp",EDGE,"E882"),sQuery(id+"F2.wireOp",EDGE,"E883"),sQuery(id+"F2.wireOp",EDGE,"E884"),sQuery(id+"F2.wireOp",EDGE,"E885"),sQuery(id+"F2.wireOp",EDGE,"E886"),sQuery(id+"F2.wireOp",EDGE,"E887"),sQuery(id+"F2.wireOp",EDGE,"E888"),sQuery(id+"F2.wireOp",EDGE,"E889"),sQuery(id+"F2.wireOp",EDGE,"E890"),sQuery(id+"F2.wireOp",EDGE,"E891"),sQuery(id+"F2.wireOp",EDGE,"E892"),sQuery(id+"F2.wireOp",EDGE,"E893"),sQuery(id+"F2.wireOp",EDGE,"E894"),sQuery(id+"F2.wireOp",EDGE,"E895"),sQuery(id+"F2.wireOp",EDGE,"E896"),sQuery(id+"F2.wireOp",EDGE,"E897"),sQuery(id+"F2.wireOp",EDGE,"E898"),sQuery(id+"F2.wireOp",EDGE,"E899"),sQuery(id+"F2.wireOp",EDGE,"E900"),sQuery(id+"F2.wireOp",EDGE,"E901"),sQuery(id+"F2.wireOp",EDGE,"E902"),sQuery(id+"F2.wireOp",EDGE,"E903"),sQuery(id+"F2.wireOp",EDGE,"E904"),sQuery(id+"F2.wireOp",EDGE,"E905"),sQuery(id+"F2.wireOp",EDGE,"E906"),sQuery(id+"F2.wireOp",EDGE,"E907"),sQuery(id+"F2.wireOp",EDGE,"E908"),sQuery(id+"F2.wireOp",EDGE,"E909"),sQuery(id+"F2.wireOp",EDGE,"E910"),sQuery(id+"F2.wireOp",EDGE,"E911"),sQuery(id+"F2.wireOp",EDGE,"E912"),sQuery(id+"F2.wireOp",EDGE,"E913"),sQuery(id+"F2.wireOp",EDGE,"E914"),sQuery(id+"F2.wireOp",EDGE,"E915"),sQuery(id+"F2.wireOp",EDGE,"E916"),sQuery(id+"F2.wireOp",EDGE,"E917"),sQuery(id+"F2.wireOp",EDGE,"E918"),sQuery(id+"F2.wireOp",EDGE,"E919"),sQuery(id+"F2.wireOp",EDGE,"E920"),sQuery(id+"F2.wireOp",EDGE,"E921"),sQuery(id+"F2.wireOp",EDGE,"E922"),sQuery(id+"F2.wireOp",EDGE,"E923"),sQuery(id+"F2.wireOp",EDGE,"E924"),sQuery(id+"F2.wireOp",EDGE,"E925"),sQuery(id+"F2.wireOp",EDGE,"E926"),sQuery(id+"F2.wireOp",EDGE,"E927"),sQuery(id+"F2.wireOp",EDGE,"E928"),sQuery(id+"F2.wireOp",EDGE,"E929"),sQuery(id+"F2.wireOp",EDGE,"E930"),sQuery(id+"F2.wireOp",EDGE,"E931"),sQuery(id+"F2.wireOp",EDGE,"E932"),sQuery(id+"F2.wireOp",EDGE,"E933"),sQuery(id+"F2.wireOp",EDGE,"E934"),sQuery(id+"F2.wireOp",EDGE,"E935"),sQuery(id+"F2.wireOp",EDGE,"E936"),sQuery(id+"F2.wireOp",EDGE,"E937"),sQuery(id+"F2.wireOp",EDGE,"E938"),sQuery(id+"F2.wireOp",EDGE,"E939"),sQuery(id+"F2.wireOp",EDGE,"E940"),sQuery(id+"F2.wireOp",EDGE,"E941"),sQuery(id+"F2.wireOp",EDGE,"E942"),sQuery(id+"F2.wireOp",EDGE,"E943"),sQuery(id+"F2.wireOp",EDGE,"E944"),sQuery(id+"F2.wireOp",EDGE,"E945"),sQuery(id+"F2.wireOp",EDGE,"E946"),sQuery(id+"F2.wireOp",EDGE,"E947"),sQuery(id+"F2.wireOp",EDGE,"E948"),sQuery(id+"F2.wireOp",EDGE,"E949"),sQuery(id+"F2.wireOp",EDGE,"E950"),sQuery(id+"F2.wireOp",EDGE,"E951"),sQuery(id+"F2.wireOp",EDGE,"E952"),sQuery(id+"F2.wireOp",EDGE,"E953"),sQuery(id+"F2.wireOp",EDGE,"E954"),sQuery(id+"F2.wireOp",EDGE,"E955")])]});
            transform(context, id + "F4", {"entities" : qUnion([Q0]), "transformType" : TransformType.TRANSLATION_3D, "dx" : 18.7 * mm, "dy" : 0 * mm, "dz" : 0 * mm, "makeCopy" : false});
        }
    });
